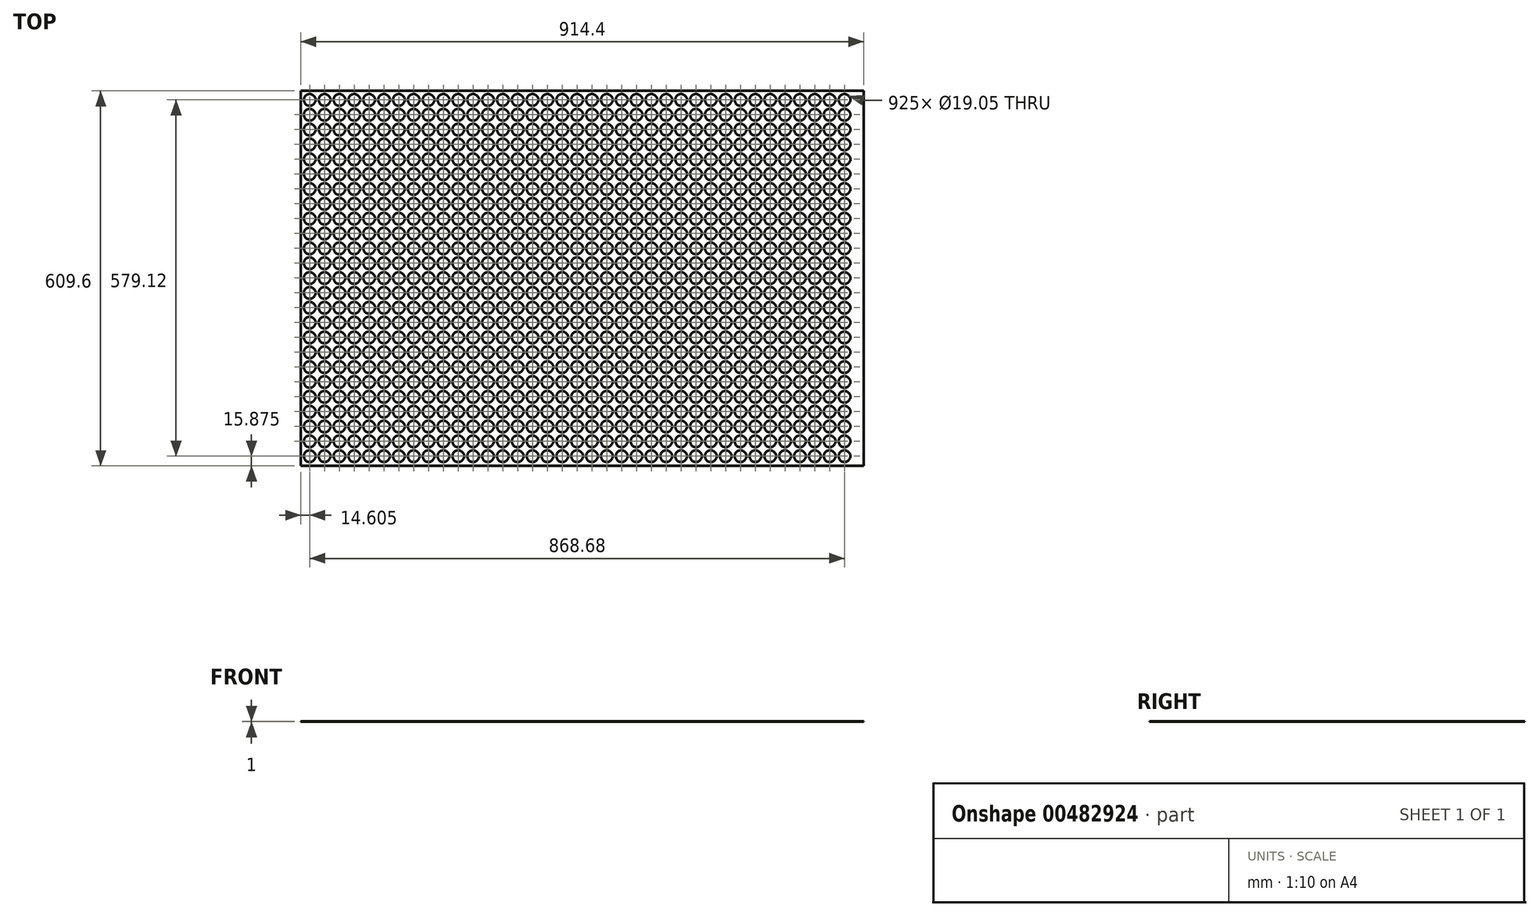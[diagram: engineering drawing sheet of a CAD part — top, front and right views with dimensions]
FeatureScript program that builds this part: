
annotation { "Feature Type Name" : "Feature", "Feature Type Description" : "" }
export const myFeature = defineFeature(function(context is Context, id is Id, definition is map)
    precondition{}
    {
        {
            var Q0;
            Q0=qCreatedBy(makeId("Top.planeOp"),FACE);
            var sketch = newSketch(context, id + "F0", { "sketchPlane" : qUnion([Q0])});
            skLineSegment(sketch, "E0.bottom", {"start": v(-457.2, 304.8) * mm, "end": v(457.2, 304.8) * mm});
            skLineSegment(sketch, "E0.top", {"start": v(-457.2, -304.8) * mm, "end": v(457.2, -304.8) * mm});
            skLineSegment(sketch, "E0.left", {"start": v(-457.2, 304.8) * mm, "end": v(-457.2, -304.8) * mm});
            skLineSegment(sketch, "E0.right", {"start": v(457.2, 304.8) * mm, "end": v(457.2, -304.8) * mm});
            skCircle(sketch, "E1", {"center": v(-442.6, 290.2) * mm, "radius": 9.53 * mm});
            skCircle(sketch, "E2.0.1.0", {"center": v(-442.6, 266.07) * mm, "radius": 9.53 * mm});
            skCircle(sketch, "E2.0.2.0", {"center": v(-442.6, 241.94) * mm, "radius": 9.53 * mm});
            skCircle(sketch, "E2.0.3.0", {"center": v(-442.6, 217.8) * mm, "radius": 9.53 * mm});
            skCircle(sketch, "E2.0.4.0", {"center": v(-442.6, 193.68) * mm, "radius": 9.53 * mm});
            skCircle(sketch, "E2.0.5.0", {"center": v(-442.6, 169.55) * mm, "radius": 9.53 * mm});
            skCircle(sketch, "E2.0.6.0", {"center": v(-442.6, 145.42) * mm, "radius": 9.53 * mm});
            skCircle(sketch, "E2.0.7.0", {"center": v(-442.6, 121.29) * mm, "radius": 9.53 * mm});
            skCircle(sketch, "E2.0.8.0", {"center": v(-442.6, 97.16) * mm, "radius": 9.53 * mm});
            skCircle(sketch, "E2.0.9.0", {"center": v(-442.6, 73.03) * mm, "radius": 9.53 * mm});
            skCircle(sketch, "E2.0.10.0", {"center": v(-442.6, 48.9) * mm, "radius": 9.53 * mm});
            skCircle(sketch, "E2.0.11.0", {"center": v(-442.6, 24.77) * mm, "radius": 9.53 * mm});
            skCircle(sketch, "E2.0.12.0", {"center": v(-442.6, 0.64) * mm, "radius": 9.53 * mm});
            skCircle(sketch, "E2.0.13.0", {"center": v(-442.6, -23.5) * mm, "radius": 9.53 * mm});
            skCircle(sketch, "E2.0.14.0", {"center": v(-442.6, -47.62) * mm, "radius": 9.53 * mm});
            skCircle(sketch, "E2.0.15.0", {"center": v(-442.6, -71.75) * mm, "radius": 9.53 * mm});
            skCircle(sketch, "E2.0.16.0", {"center": v(-442.6, -95.88) * mm, "radius": 9.53 * mm});
            skCircle(sketch, "E2.0.17.0", {"center": v(-442.6, -120.01) * mm, "radius": 9.53 * mm});
            skCircle(sketch, "E2.0.18.0", {"center": v(-442.6, -144.14) * mm, "radius": 9.53 * mm});
            skCircle(sketch, "E2.0.19.0", {"center": v(-442.6, -168.27) * mm, "radius": 9.53 * mm});
            skCircle(sketch, "E2.0.20.0", {"center": v(-442.6, -192.4) * mm, "radius": 9.53 * mm});
            skCircle(sketch, "E2.0.21.0", {"center": v(-442.6, -216.53) * mm, "radius": 9.53 * mm});
            skCircle(sketch, "E2.0.22.0", {"center": v(-442.6, -240.66) * mm, "radius": 9.53 * mm});
            skCircle(sketch, "E2.0.23.0", {"center": v(-442.6, -264.8) * mm, "radius": 9.53 * mm});
            skCircle(sketch, "E2.0.24.0", {"center": v(-442.6, -288.92) * mm, "radius": 9.53 * mm});
            skCircle(sketch, "E2.1.0.0", {"center": v(-418.47, 290.2) * mm, "radius": 9.53 * mm});
            skCircle(sketch, "E2.1.1.0", {"center": v(-418.47, 266.07) * mm, "radius": 9.53 * mm});
            skCircle(sketch, "E2.1.2.0", {"center": v(-418.47, 241.94) * mm, "radius": 9.53 * mm});
            skCircle(sketch, "E2.1.3.0", {"center": v(-418.47, 217.8) * mm, "radius": 9.53 * mm});
            skCircle(sketch, "E2.1.4.0", {"center": v(-418.47, 193.68) * mm, "radius": 9.53 * mm});
            skCircle(sketch, "E2.1.5.0", {"center": v(-418.47, 169.55) * mm, "radius": 9.53 * mm});
            skCircle(sketch, "E2.1.6.0", {"center": v(-418.47, 145.42) * mm, "radius": 9.53 * mm});
            skCircle(sketch, "E2.1.7.0", {"center": v(-418.47, 121.29) * mm, "radius": 9.53 * mm});
            skCircle(sketch, "E2.1.8.0", {"center": v(-418.47, 97.16) * mm, "radius": 9.53 * mm});
            skCircle(sketch, "E2.1.9.0", {"center": v(-418.47, 73.03) * mm, "radius": 9.53 * mm});
            skCircle(sketch, "E2.1.10.0", {"center": v(-418.47, 48.9) * mm, "radius": 9.53 * mm});
            skCircle(sketch, "E2.1.11.0", {"center": v(-418.47, 24.77) * mm, "radius": 9.53 * mm});
            skCircle(sketch, "E2.1.12.0", {"center": v(-418.47, 0.64) * mm, "radius": 9.53 * mm});
            skCircle(sketch, "E2.1.13.0", {"center": v(-418.47, -23.5) * mm, "radius": 9.53 * mm});
            skCircle(sketch, "E2.1.14.0", {"center": v(-418.47, -47.62) * mm, "radius": 9.53 * mm});
            skCircle(sketch, "E2.1.15.0", {"center": v(-418.47, -71.75) * mm, "radius": 9.53 * mm});
            skCircle(sketch, "E2.1.16.0", {"center": v(-418.47, -95.88) * mm, "radius": 9.53 * mm});
            skCircle(sketch, "E2.1.17.0", {"center": v(-418.47, -120.01) * mm, "radius": 9.53 * mm});
            skCircle(sketch, "E2.1.18.0", {"center": v(-418.47, -144.14) * mm, "radius": 9.53 * mm});
            skCircle(sketch, "E2.1.19.0", {"center": v(-418.47, -168.27) * mm, "radius": 9.53 * mm});
            skCircle(sketch, "E2.1.20.0", {"center": v(-418.47, -192.4) * mm, "radius": 9.53 * mm});
            skCircle(sketch, "E2.1.21.0", {"center": v(-418.47, -216.53) * mm, "radius": 9.53 * mm});
            skCircle(sketch, "E2.1.22.0", {"center": v(-418.47, -240.66) * mm, "radius": 9.53 * mm});
            skCircle(sketch, "E2.1.23.0", {"center": v(-418.47, -264.8) * mm, "radius": 9.53 * mm});
            skCircle(sketch, "E2.1.24.0", {"center": v(-418.47, -288.92) * mm, "radius": 9.53 * mm});
            skCircle(sketch, "E2.2.0.0", {"center": v(-394.34, 290.2) * mm, "radius": 9.53 * mm});
            skCircle(sketch, "E2.2.1.0", {"center": v(-394.34, 266.07) * mm, "radius": 9.53 * mm});
            skCircle(sketch, "E2.2.2.0", {"center": v(-394.34, 241.94) * mm, "radius": 9.53 * mm});
            skCircle(sketch, "E2.2.3.0", {"center": v(-394.34, 217.8) * mm, "radius": 9.53 * mm});
            skCircle(sketch, "E2.2.4.0", {"center": v(-394.34, 193.68) * mm, "radius": 9.53 * mm});
            skCircle(sketch, "E2.2.5.0", {"center": v(-394.34, 169.55) * mm, "radius": 9.53 * mm});
            skCircle(sketch, "E2.2.6.0", {"center": v(-394.34, 145.42) * mm, "radius": 9.53 * mm});
            skCircle(sketch, "E2.2.7.0", {"center": v(-394.34, 121.29) * mm, "radius": 9.53 * mm});
            skCircle(sketch, "E2.2.8.0", {"center": v(-394.34, 97.16) * mm, "radius": 9.53 * mm});
            skCircle(sketch, "E2.2.9.0", {"center": v(-394.34, 73.03) * mm, "radius": 9.53 * mm});
            skCircle(sketch, "E2.2.10.0", {"center": v(-394.34, 48.9) * mm, "radius": 9.53 * mm});
            skCircle(sketch, "E2.2.11.0", {"center": v(-394.34, 24.77) * mm, "radius": 9.53 * mm});
            skCircle(sketch, "E2.2.12.0", {"center": v(-394.34, 0.64) * mm, "radius": 9.53 * mm});
            skCircle(sketch, "E2.2.13.0", {"center": v(-394.34, -23.5) * mm, "radius": 9.53 * mm});
            skCircle(sketch, "E2.2.14.0", {"center": v(-394.34, -47.62) * mm, "radius": 9.53 * mm});
            skCircle(sketch, "E2.2.15.0", {"center": v(-394.34, -71.75) * mm, "radius": 9.53 * mm});
            skCircle(sketch, "E2.2.16.0", {"center": v(-394.34, -95.88) * mm, "radius": 9.53 * mm});
            skCircle(sketch, "E2.2.17.0", {"center": v(-394.34, -120.01) * mm, "radius": 9.53 * mm});
            skCircle(sketch, "E2.2.18.0", {"center": v(-394.34, -144.14) * mm, "radius": 9.53 * mm});
            skCircle(sketch, "E2.2.19.0", {"center": v(-394.34, -168.27) * mm, "radius": 9.53 * mm});
            skCircle(sketch, "E2.2.20.0", {"center": v(-394.34, -192.4) * mm, "radius": 9.53 * mm});
            skCircle(sketch, "E2.2.21.0", {"center": v(-394.34, -216.53) * mm, "radius": 9.53 * mm});
            skCircle(sketch, "E2.2.22.0", {"center": v(-394.34, -240.66) * mm, "radius": 9.53 * mm});
            skCircle(sketch, "E2.2.23.0", {"center": v(-394.34, -264.8) * mm, "radius": 9.53 * mm});
            skCircle(sketch, "E2.2.24.0", {"center": v(-394.34, -288.92) * mm, "radius": 9.53 * mm});
            skCircle(sketch, "E2.3.0.0", {"center": v(-370.2, 290.2) * mm, "radius": 9.53 * mm});
            skCircle(sketch, "E2.3.1.0", {"center": v(-370.2, 266.07) * mm, "radius": 9.53 * mm});
            skCircle(sketch, "E2.3.2.0", {"center": v(-370.2, 241.94) * mm, "radius": 9.53 * mm});
            skCircle(sketch, "E2.3.3.0", {"center": v(-370.2, 217.8) * mm, "radius": 9.53 * mm});
            skCircle(sketch, "E2.3.4.0", {"center": v(-370.2, 193.68) * mm, "radius": 9.53 * mm});
            skCircle(sketch, "E2.3.5.0", {"center": v(-370.2, 169.55) * mm, "radius": 9.53 * mm});
            skCircle(sketch, "E2.3.6.0", {"center": v(-370.2, 145.42) * mm, "radius": 9.53 * mm});
            skCircle(sketch, "E2.3.7.0", {"center": v(-370.2, 121.29) * mm, "radius": 9.53 * mm});
            skCircle(sketch, "E2.3.8.0", {"center": v(-370.2, 97.16) * mm, "radius": 9.53 * mm});
            skCircle(sketch, "E2.3.9.0", {"center": v(-370.2, 73.03) * mm, "radius": 9.53 * mm});
            skCircle(sketch, "E2.3.10.0", {"center": v(-370.2, 48.9) * mm, "radius": 9.53 * mm});
            skCircle(sketch, "E2.3.11.0", {"center": v(-370.2, 24.77) * mm, "radius": 9.53 * mm});
            skCircle(sketch, "E2.3.12.0", {"center": v(-370.2, 0.64) * mm, "radius": 9.53 * mm});
            skCircle(sketch, "E2.3.13.0", {"center": v(-370.2, -23.5) * mm, "radius": 9.53 * mm});
            skCircle(sketch, "E2.3.14.0", {"center": v(-370.2, -47.62) * mm, "radius": 9.53 * mm});
            skCircle(sketch, "E2.3.15.0", {"center": v(-370.2, -71.75) * mm, "radius": 9.53 * mm});
            skCircle(sketch, "E2.3.16.0", {"center": v(-370.2, -95.88) * mm, "radius": 9.53 * mm});
            skCircle(sketch, "E2.3.17.0", {"center": v(-370.2, -120.01) * mm, "radius": 9.53 * mm});
            skCircle(sketch, "E2.3.18.0", {"center": v(-370.2, -144.14) * mm, "radius": 9.53 * mm});
            skCircle(sketch, "E2.3.19.0", {"center": v(-370.2, -168.27) * mm, "radius": 9.53 * mm});
            skCircle(sketch, "E2.3.20.0", {"center": v(-370.2, -192.4) * mm, "radius": 9.53 * mm});
            skCircle(sketch, "E2.3.21.0", {"center": v(-370.2, -216.53) * mm, "radius": 9.53 * mm});
            skCircle(sketch, "E2.3.22.0", {"center": v(-370.2, -240.66) * mm, "radius": 9.53 * mm});
            skCircle(sketch, "E2.3.23.0", {"center": v(-370.2, -264.8) * mm, "radius": 9.53 * mm});
            skCircle(sketch, "E2.3.24.0", {"center": v(-370.2, -288.92) * mm, "radius": 9.53 * mm});
            skCircle(sketch, "E2.4.0.0", {"center": v(-346.08, 290.2) * mm, "radius": 9.53 * mm});
            skCircle(sketch, "E2.4.1.0", {"center": v(-346.08, 266.07) * mm, "radius": 9.53 * mm});
            skCircle(sketch, "E2.4.2.0", {"center": v(-346.08, 241.94) * mm, "radius": 9.53 * mm});
            skCircle(sketch, "E2.4.3.0", {"center": v(-346.08, 217.8) * mm, "radius": 9.53 * mm});
            skCircle(sketch, "E2.4.4.0", {"center": v(-346.08, 193.68) * mm, "radius": 9.53 * mm});
            skCircle(sketch, "E2.4.5.0", {"center": v(-346.08, 169.55) * mm, "radius": 9.53 * mm});
            skCircle(sketch, "E2.4.6.0", {"center": v(-346.08, 145.42) * mm, "radius": 9.53 * mm});
            skCircle(sketch, "E2.4.7.0", {"center": v(-346.08, 121.29) * mm, "radius": 9.53 * mm});
            skCircle(sketch, "E2.4.8.0", {"center": v(-346.08, 97.16) * mm, "radius": 9.53 * mm});
            skCircle(sketch, "E2.4.9.0", {"center": v(-346.08, 73.03) * mm, "radius": 9.53 * mm});
            skCircle(sketch, "E2.4.10.0", {"center": v(-346.08, 48.9) * mm, "radius": 9.53 * mm});
            skCircle(sketch, "E2.4.11.0", {"center": v(-346.08, 24.77) * mm, "radius": 9.53 * mm});
            skCircle(sketch, "E2.4.12.0", {"center": v(-346.08, 0.64) * mm, "radius": 9.53 * mm});
            skCircle(sketch, "E2.4.13.0", {"center": v(-346.08, -23.5) * mm, "radius": 9.53 * mm});
            skCircle(sketch, "E2.4.14.0", {"center": v(-346.08, -47.62) * mm, "radius": 9.53 * mm});
            skCircle(sketch, "E2.4.15.0", {"center": v(-346.08, -71.75) * mm, "radius": 9.53 * mm});
            skCircle(sketch, "E2.4.16.0", {"center": v(-346.08, -95.88) * mm, "radius": 9.53 * mm});
            skCircle(sketch, "E2.4.17.0", {"center": v(-346.08, -120.01) * mm, "radius": 9.53 * mm});
            skCircle(sketch, "E2.4.18.0", {"center": v(-346.08, -144.14) * mm, "radius": 9.53 * mm});
            skCircle(sketch, "E2.4.19.0", {"center": v(-346.08, -168.27) * mm, "radius": 9.53 * mm});
            skCircle(sketch, "E2.4.20.0", {"center": v(-346.08, -192.4) * mm, "radius": 9.53 * mm});
            skCircle(sketch, "E2.4.21.0", {"center": v(-346.08, -216.53) * mm, "radius": 9.53 * mm});
            skCircle(sketch, "E2.4.22.0", {"center": v(-346.08, -240.66) * mm, "radius": 9.53 * mm});
            skCircle(sketch, "E2.4.23.0", {"center": v(-346.08, -264.8) * mm, "radius": 9.53 * mm});
            skCircle(sketch, "E2.4.24.0", {"center": v(-346.08, -288.92) * mm, "radius": 9.53 * mm});
            skCircle(sketch, "E2.5.0.0", {"center": v(-321.95, 290.2) * mm, "radius": 9.53 * mm});
            skCircle(sketch, "E2.5.1.0", {"center": v(-321.95, 266.07) * mm, "radius": 9.53 * mm});
            skCircle(sketch, "E2.5.2.0", {"center": v(-321.95, 241.94) * mm, "radius": 9.53 * mm});
            skCircle(sketch, "E2.5.3.0", {"center": v(-321.95, 217.8) * mm, "radius": 9.53 * mm});
            skCircle(sketch, "E2.5.4.0", {"center": v(-321.95, 193.68) * mm, "radius": 9.53 * mm});
            skCircle(sketch, "E2.5.5.0", {"center": v(-321.95, 169.55) * mm, "radius": 9.53 * mm});
            skCircle(sketch, "E2.5.6.0", {"center": v(-321.95, 145.42) * mm, "radius": 9.53 * mm});
            skCircle(sketch, "E2.5.7.0", {"center": v(-321.95, 121.29) * mm, "radius": 9.53 * mm});
            skCircle(sketch, "E2.5.8.0", {"center": v(-321.95, 97.16) * mm, "radius": 9.53 * mm});
            skCircle(sketch, "E2.5.9.0", {"center": v(-321.95, 73.03) * mm, "radius": 9.53 * mm});
            skCircle(sketch, "E2.5.10.0", {"center": v(-321.95, 48.9) * mm, "radius": 9.53 * mm});
            skCircle(sketch, "E2.5.11.0", {"center": v(-321.95, 24.77) * mm, "radius": 9.53 * mm});
            skCircle(sketch, "E2.5.12.0", {"center": v(-321.95, 0.64) * mm, "radius": 9.53 * mm});
            skCircle(sketch, "E2.5.13.0", {"center": v(-321.95, -23.5) * mm, "radius": 9.53 * mm});
            skCircle(sketch, "E2.5.14.0", {"center": v(-321.95, -47.62) * mm, "radius": 9.53 * mm});
            skCircle(sketch, "E2.5.15.0", {"center": v(-321.95, -71.75) * mm, "radius": 9.53 * mm});
            skCircle(sketch, "E2.5.16.0", {"center": v(-321.95, -95.88) * mm, "radius": 9.53 * mm});
            skCircle(sketch, "E2.5.17.0", {"center": v(-321.95, -120.01) * mm, "radius": 9.53 * mm});
            skCircle(sketch, "E2.5.18.0", {"center": v(-321.95, -144.14) * mm, "radius": 9.53 * mm});
            skCircle(sketch, "E2.5.19.0", {"center": v(-321.95, -168.27) * mm, "radius": 9.53 * mm});
            skCircle(sketch, "E2.5.20.0", {"center": v(-321.95, -192.4) * mm, "radius": 9.53 * mm});
            skCircle(sketch, "E2.5.21.0", {"center": v(-321.95, -216.53) * mm, "radius": 9.53 * mm});
            skCircle(sketch, "E2.5.22.0", {"center": v(-321.95, -240.66) * mm, "radius": 9.53 * mm});
            skCircle(sketch, "E2.5.23.0", {"center": v(-321.95, -264.8) * mm, "radius": 9.53 * mm});
            skCircle(sketch, "E2.5.24.0", {"center": v(-321.95, -288.92) * mm, "radius": 9.53 * mm});
            skCircle(sketch, "E2.6.0.0", {"center": v(-297.82, 290.2) * mm, "radius": 9.53 * mm});
            skCircle(sketch, "E2.6.1.0", {"center": v(-297.82, 266.07) * mm, "radius": 9.53 * mm});
            skCircle(sketch, "E2.6.2.0", {"center": v(-297.82, 241.94) * mm, "radius": 9.53 * mm});
            skCircle(sketch, "E2.6.3.0", {"center": v(-297.82, 217.8) * mm, "radius": 9.53 * mm});
            skCircle(sketch, "E2.6.4.0", {"center": v(-297.82, 193.68) * mm, "radius": 9.53 * mm});
            skCircle(sketch, "E2.6.5.0", {"center": v(-297.82, 169.55) * mm, "radius": 9.53 * mm});
            skCircle(sketch, "E2.6.6.0", {"center": v(-297.82, 145.42) * mm, "radius": 9.53 * mm});
            skCircle(sketch, "E2.6.7.0", {"center": v(-297.82, 121.29) * mm, "radius": 9.53 * mm});
            skCircle(sketch, "E2.6.8.0", {"center": v(-297.82, 97.16) * mm, "radius": 9.53 * mm});
            skCircle(sketch, "E2.6.9.0", {"center": v(-297.82, 73.03) * mm, "radius": 9.53 * mm});
            skCircle(sketch, "E2.6.10.0", {"center": v(-297.82, 48.9) * mm, "radius": 9.53 * mm});
            skCircle(sketch, "E2.6.11.0", {"center": v(-297.82, 24.77) * mm, "radius": 9.53 * mm});
            skCircle(sketch, "E2.6.12.0", {"center": v(-297.82, 0.64) * mm, "radius": 9.53 * mm});
            skCircle(sketch, "E2.6.13.0", {"center": v(-297.82, -23.5) * mm, "radius": 9.53 * mm});
            skCircle(sketch, "E2.6.14.0", {"center": v(-297.82, -47.62) * mm, "radius": 9.53 * mm});
            skCircle(sketch, "E2.6.15.0", {"center": v(-297.82, -71.75) * mm, "radius": 9.53 * mm});
            skCircle(sketch, "E2.6.16.0", {"center": v(-297.82, -95.88) * mm, "radius": 9.53 * mm});
            skCircle(sketch, "E2.6.17.0", {"center": v(-297.82, -120.01) * mm, "radius": 9.53 * mm});
            skCircle(sketch, "E2.6.18.0", {"center": v(-297.82, -144.14) * mm, "radius": 9.53 * mm});
            skCircle(sketch, "E2.6.19.0", {"center": v(-297.82, -168.27) * mm, "radius": 9.53 * mm});
            skCircle(sketch, "E2.6.20.0", {"center": v(-297.82, -192.4) * mm, "radius": 9.53 * mm});
            skCircle(sketch, "E2.6.21.0", {"center": v(-297.82, -216.53) * mm, "radius": 9.53 * mm});
            skCircle(sketch, "E2.6.22.0", {"center": v(-297.82, -240.66) * mm, "radius": 9.53 * mm});
            skCircle(sketch, "E2.6.23.0", {"center": v(-297.82, -264.8) * mm, "radius": 9.53 * mm});
            skCircle(sketch, "E2.6.24.0", {"center": v(-297.82, -288.92) * mm, "radius": 9.53 * mm});
            skCircle(sketch, "E2.7.0.0", {"center": v(-273.69, 290.2) * mm, "radius": 9.53 * mm});
            skCircle(sketch, "E2.7.1.0", {"center": v(-273.69, 266.07) * mm, "radius": 9.53 * mm});
            skCircle(sketch, "E2.7.2.0", {"center": v(-273.69, 241.94) * mm, "radius": 9.53 * mm});
            skCircle(sketch, "E2.7.3.0", {"center": v(-273.69, 217.8) * mm, "radius": 9.53 * mm});
            skCircle(sketch, "E2.7.4.0", {"center": v(-273.69, 193.68) * mm, "radius": 9.53 * mm});
            skCircle(sketch, "E2.7.5.0", {"center": v(-273.69, 169.55) * mm, "radius": 9.53 * mm});
            skCircle(sketch, "E2.7.6.0", {"center": v(-273.69, 145.42) * mm, "radius": 9.53 * mm});
            skCircle(sketch, "E2.7.7.0", {"center": v(-273.69, 121.29) * mm, "radius": 9.53 * mm});
            skCircle(sketch, "E2.7.8.0", {"center": v(-273.69, 97.16) * mm, "radius": 9.53 * mm});
            skCircle(sketch, "E2.7.9.0", {"center": v(-273.69, 73.03) * mm, "radius": 9.53 * mm});
            skCircle(sketch, "E2.7.10.0", {"center": v(-273.69, 48.9) * mm, "radius": 9.53 * mm});
            skCircle(sketch, "E2.7.11.0", {"center": v(-273.69, 24.77) * mm, "radius": 9.53 * mm});
            skCircle(sketch, "E2.7.12.0", {"center": v(-273.69, 0.64) * mm, "radius": 9.53 * mm});
            skCircle(sketch, "E2.7.13.0", {"center": v(-273.69, -23.5) * mm, "radius": 9.53 * mm});
            skCircle(sketch, "E2.7.14.0", {"center": v(-273.69, -47.62) * mm, "radius": 9.53 * mm});
            skCircle(sketch, "E2.7.15.0", {"center": v(-273.69, -71.75) * mm, "radius": 9.53 * mm});
            skCircle(sketch, "E2.7.16.0", {"center": v(-273.69, -95.88) * mm, "radius": 9.53 * mm});
            skCircle(sketch, "E2.7.17.0", {"center": v(-273.69, -120.01) * mm, "radius": 9.53 * mm});
            skCircle(sketch, "E2.7.18.0", {"center": v(-273.69, -144.14) * mm, "radius": 9.53 * mm});
            skCircle(sketch, "E2.7.19.0", {"center": v(-273.69, -168.27) * mm, "radius": 9.53 * mm});
            skCircle(sketch, "E2.7.20.0", {"center": v(-273.69, -192.4) * mm, "radius": 9.53 * mm});
            skCircle(sketch, "E2.7.21.0", {"center": v(-273.69, -216.53) * mm, "radius": 9.53 * mm});
            skCircle(sketch, "E2.7.22.0", {"center": v(-273.69, -240.66) * mm, "radius": 9.53 * mm});
            skCircle(sketch, "E2.7.23.0", {"center": v(-273.69, -264.8) * mm, "radius": 9.53 * mm});
            skCircle(sketch, "E2.7.24.0", {"center": v(-273.69, -288.92) * mm, "radius": 9.53 * mm});
            skCircle(sketch, "E2.8.0.0", {"center": v(-249.56, 290.2) * mm, "radius": 9.53 * mm});
            skCircle(sketch, "E2.8.1.0", {"center": v(-249.56, 266.07) * mm, "radius": 9.53 * mm});
            skCircle(sketch, "E2.8.2.0", {"center": v(-249.56, 241.94) * mm, "radius": 9.53 * mm});
            skCircle(sketch, "E2.8.3.0", {"center": v(-249.56, 217.8) * mm, "radius": 9.53 * mm});
            skCircle(sketch, "E2.8.4.0", {"center": v(-249.56, 193.68) * mm, "radius": 9.53 * mm});
            skCircle(sketch, "E2.8.5.0", {"center": v(-249.56, 169.55) * mm, "radius": 9.53 * mm});
            skCircle(sketch, "E2.8.6.0", {"center": v(-249.56, 145.42) * mm, "radius": 9.53 * mm});
            skCircle(sketch, "E2.8.7.0", {"center": v(-249.56, 121.29) * mm, "radius": 9.53 * mm});
            skCircle(sketch, "E2.8.8.0", {"center": v(-249.56, 97.16) * mm, "radius": 9.53 * mm});
            skCircle(sketch, "E2.8.9.0", {"center": v(-249.56, 73.03) * mm, "radius": 9.53 * mm});
            skCircle(sketch, "E2.8.10.0", {"center": v(-249.56, 48.9) * mm, "radius": 9.53 * mm});
            skCircle(sketch, "E2.8.11.0", {"center": v(-249.56, 24.77) * mm, "radius": 9.53 * mm});
            skCircle(sketch, "E2.8.12.0", {"center": v(-249.56, 0.64) * mm, "radius": 9.53 * mm});
            skCircle(sketch, "E2.8.13.0", {"center": v(-249.56, -23.5) * mm, "radius": 9.53 * mm});
            skCircle(sketch, "E2.8.14.0", {"center": v(-249.56, -47.62) * mm, "radius": 9.53 * mm});
            skCircle(sketch, "E2.8.15.0", {"center": v(-249.56, -71.75) * mm, "radius": 9.53 * mm});
            skCircle(sketch, "E2.8.16.0", {"center": v(-249.56, -95.88) * mm, "radius": 9.53 * mm});
            skCircle(sketch, "E2.8.17.0", {"center": v(-249.56, -120.01) * mm, "radius": 9.53 * mm});
            skCircle(sketch, "E2.8.18.0", {"center": v(-249.56, -144.14) * mm, "radius": 9.53 * mm});
            skCircle(sketch, "E2.8.19.0", {"center": v(-249.56, -168.27) * mm, "radius": 9.53 * mm});
            skCircle(sketch, "E2.8.20.0", {"center": v(-249.56, -192.4) * mm, "radius": 9.53 * mm});
            skCircle(sketch, "E2.8.21.0", {"center": v(-249.56, -216.53) * mm, "radius": 9.53 * mm});
            skCircle(sketch, "E2.8.22.0", {"center": v(-249.56, -240.66) * mm, "radius": 9.53 * mm});
            skCircle(sketch, "E2.8.23.0", {"center": v(-249.56, -264.8) * mm, "radius": 9.53 * mm});
            skCircle(sketch, "E2.8.24.0", {"center": v(-249.56, -288.92) * mm, "radius": 9.53 * mm});
            skCircle(sketch, "E2.9.0.0", {"center": v(-225.43, 290.2) * mm, "radius": 9.53 * mm});
            skCircle(sketch, "E2.9.1.0", {"center": v(-225.43, 266.07) * mm, "radius": 9.53 * mm});
            skCircle(sketch, "E2.9.2.0", {"center": v(-225.43, 241.94) * mm, "radius": 9.53 * mm});
            skCircle(sketch, "E2.9.3.0", {"center": v(-225.43, 217.8) * mm, "radius": 9.53 * mm});
            skCircle(sketch, "E2.9.4.0", {"center": v(-225.43, 193.68) * mm, "radius": 9.53 * mm});
            skCircle(sketch, "E2.9.5.0", {"center": v(-225.43, 169.55) * mm, "radius": 9.53 * mm});
            skCircle(sketch, "E2.9.6.0", {"center": v(-225.43, 145.42) * mm, "radius": 9.53 * mm});
            skCircle(sketch, "E2.9.7.0", {"center": v(-225.43, 121.29) * mm, "radius": 9.53 * mm});
            skCircle(sketch, "E2.9.8.0", {"center": v(-225.43, 97.16) * mm, "radius": 9.53 * mm});
            skCircle(sketch, "E2.9.9.0", {"center": v(-225.43, 73.03) * mm, "radius": 9.53 * mm});
            skCircle(sketch, "E2.9.10.0", {"center": v(-225.43, 48.9) * mm, "radius": 9.53 * mm});
            skCircle(sketch, "E2.9.11.0", {"center": v(-225.43, 24.77) * mm, "radius": 9.53 * mm});
            skCircle(sketch, "E2.9.12.0", {"center": v(-225.43, 0.64) * mm, "radius": 9.53 * mm});
            skCircle(sketch, "E2.9.13.0", {"center": v(-225.43, -23.5) * mm, "radius": 9.53 * mm});
            skCircle(sketch, "E2.9.14.0", {"center": v(-225.43, -47.62) * mm, "radius": 9.53 * mm});
            skCircle(sketch, "E2.9.15.0", {"center": v(-225.43, -71.75) * mm, "radius": 9.53 * mm});
            skCircle(sketch, "E2.9.16.0", {"center": v(-225.43, -95.88) * mm, "radius": 9.53 * mm});
            skCircle(sketch, "E2.9.17.0", {"center": v(-225.43, -120.01) * mm, "radius": 9.53 * mm});
            skCircle(sketch, "E2.9.18.0", {"center": v(-225.43, -144.14) * mm, "radius": 9.53 * mm});
            skCircle(sketch, "E2.9.19.0", {"center": v(-225.43, -168.27) * mm, "radius": 9.53 * mm});
            skCircle(sketch, "E2.9.20.0", {"center": v(-225.43, -192.4) * mm, "radius": 9.53 * mm});
            skCircle(sketch, "E2.9.21.0", {"center": v(-225.43, -216.53) * mm, "radius": 9.53 * mm});
            skCircle(sketch, "E2.9.22.0", {"center": v(-225.43, -240.66) * mm, "radius": 9.53 * mm});
            skCircle(sketch, "E2.9.23.0", {"center": v(-225.43, -264.8) * mm, "radius": 9.53 * mm});
            skCircle(sketch, "E2.9.24.0", {"center": v(-225.43, -288.92) * mm, "radius": 9.53 * mm});
            skCircle(sketch, "E2.10.0.0", {"center": v(-201.3, 290.2) * mm, "radius": 9.53 * mm});
            skCircle(sketch, "E2.10.1.0", {"center": v(-201.3, 266.07) * mm, "radius": 9.53 * mm});
            skCircle(sketch, "E2.10.2.0", {"center": v(-201.3, 241.94) * mm, "radius": 9.53 * mm});
            skCircle(sketch, "E2.10.3.0", {"center": v(-201.3, 217.8) * mm, "radius": 9.53 * mm});
            skCircle(sketch, "E2.10.4.0", {"center": v(-201.3, 193.68) * mm, "radius": 9.53 * mm});
            skCircle(sketch, "E2.10.5.0", {"center": v(-201.3, 169.55) * mm, "radius": 9.53 * mm});
            skCircle(sketch, "E2.10.6.0", {"center": v(-201.3, 145.42) * mm, "radius": 9.53 * mm});
            skCircle(sketch, "E2.10.7.0", {"center": v(-201.3, 121.29) * mm, "radius": 9.53 * mm});
            skCircle(sketch, "E2.10.8.0", {"center": v(-201.3, 97.16) * mm, "radius": 9.53 * mm});
            skCircle(sketch, "E2.10.9.0", {"center": v(-201.3, 73.03) * mm, "radius": 9.53 * mm});
            skCircle(sketch, "E2.10.10.0", {"center": v(-201.3, 48.9) * mm, "radius": 9.53 * mm});
            skCircle(sketch, "E2.10.11.0", {"center": v(-201.3, 24.77) * mm, "radius": 9.53 * mm});
            skCircle(sketch, "E2.10.12.0", {"center": v(-201.3, 0.64) * mm, "radius": 9.53 * mm});
            skCircle(sketch, "E2.10.13.0", {"center": v(-201.3, -23.5) * mm, "radius": 9.53 * mm});
            skCircle(sketch, "E2.10.14.0", {"center": v(-201.3, -47.62) * mm, "radius": 9.53 * mm});
            skCircle(sketch, "E2.10.15.0", {"center": v(-201.3, -71.75) * mm, "radius": 9.53 * mm});
            skCircle(sketch, "E2.10.16.0", {"center": v(-201.3, -95.88) * mm, "radius": 9.53 * mm});
            skCircle(sketch, "E2.10.17.0", {"center": v(-201.3, -120.01) * mm, "radius": 9.53 * mm});
            skCircle(sketch, "E2.10.18.0", {"center": v(-201.3, -144.14) * mm, "radius": 9.53 * mm});
            skCircle(sketch, "E2.10.19.0", {"center": v(-201.3, -168.27) * mm, "radius": 9.53 * mm});
            skCircle(sketch, "E2.10.20.0", {"center": v(-201.3, -192.4) * mm, "radius": 9.53 * mm});
            skCircle(sketch, "E2.10.21.0", {"center": v(-201.3, -216.53) * mm, "radius": 9.53 * mm});
            skCircle(sketch, "E2.10.22.0", {"center": v(-201.3, -240.66) * mm, "radius": 9.53 * mm});
            skCircle(sketch, "E2.10.23.0", {"center": v(-201.3, -264.8) * mm, "radius": 9.53 * mm});
            skCircle(sketch, "E2.10.24.0", {"center": v(-201.3, -288.92) * mm, "radius": 9.53 * mm});
            skCircle(sketch, "E2.11.0.0", {"center": v(-177.17, 290.2) * mm, "radius": 9.53 * mm});
            skCircle(sketch, "E2.11.1.0", {"center": v(-177.17, 266.07) * mm, "radius": 9.53 * mm});
            skCircle(sketch, "E2.11.2.0", {"center": v(-177.17, 241.94) * mm, "radius": 9.53 * mm});
            skCircle(sketch, "E2.11.3.0", {"center": v(-177.17, 217.8) * mm, "radius": 9.53 * mm});
            skCircle(sketch, "E2.11.4.0", {"center": v(-177.17, 193.68) * mm, "radius": 9.53 * mm});
            skCircle(sketch, "E2.11.5.0", {"center": v(-177.17, 169.55) * mm, "radius": 9.53 * mm});
            skCircle(sketch, "E2.11.6.0", {"center": v(-177.17, 145.42) * mm, "radius": 9.53 * mm});
            skCircle(sketch, "E2.11.7.0", {"center": v(-177.17, 121.29) * mm, "radius": 9.53 * mm});
            skCircle(sketch, "E2.11.8.0", {"center": v(-177.17, 97.16) * mm, "radius": 9.53 * mm});
            skCircle(sketch, "E2.11.9.0", {"center": v(-177.17, 73.03) * mm, "radius": 9.53 * mm});
            skCircle(sketch, "E2.11.10.0", {"center": v(-177.17, 48.9) * mm, "radius": 9.53 * mm});
            skCircle(sketch, "E2.11.11.0", {"center": v(-177.17, 24.77) * mm, "radius": 9.53 * mm});
            skCircle(sketch, "E2.11.12.0", {"center": v(-177.17, 0.64) * mm, "radius": 9.53 * mm});
            skCircle(sketch, "E2.11.13.0", {"center": v(-177.17, -23.5) * mm, "radius": 9.53 * mm});
            skCircle(sketch, "E2.11.14.0", {"center": v(-177.17, -47.62) * mm, "radius": 9.53 * mm});
            skCircle(sketch, "E2.11.15.0", {"center": v(-177.17, -71.75) * mm, "radius": 9.53 * mm});
            skCircle(sketch, "E2.11.16.0", {"center": v(-177.17, -95.88) * mm, "radius": 9.53 * mm});
            skCircle(sketch, "E2.11.17.0", {"center": v(-177.17, -120.01) * mm, "radius": 9.53 * mm});
            skCircle(sketch, "E2.11.18.0", {"center": v(-177.17, -144.14) * mm, "radius": 9.53 * mm});
            skCircle(sketch, "E2.11.19.0", {"center": v(-177.17, -168.27) * mm, "radius": 9.53 * mm});
            skCircle(sketch, "E2.11.20.0", {"center": v(-177.17, -192.4) * mm, "radius": 9.53 * mm});
            skCircle(sketch, "E2.11.21.0", {"center": v(-177.17, -216.53) * mm, "radius": 9.53 * mm});
            skCircle(sketch, "E2.11.22.0", {"center": v(-177.17, -240.66) * mm, "radius": 9.53 * mm});
            skCircle(sketch, "E2.11.23.0", {"center": v(-177.17, -264.8) * mm, "radius": 9.53 * mm});
            skCircle(sketch, "E2.11.24.0", {"center": v(-177.17, -288.92) * mm, "radius": 9.53 * mm});
            skCircle(sketch, "E2.12.0.0", {"center": v(-153.04, 290.2) * mm, "radius": 9.53 * mm});
            skCircle(sketch, "E2.12.1.0", {"center": v(-153.04, 266.07) * mm, "radius": 9.53 * mm});
            skCircle(sketch, "E2.12.2.0", {"center": v(-153.04, 241.94) * mm, "radius": 9.53 * mm});
            skCircle(sketch, "E2.12.3.0", {"center": v(-153.04, 217.8) * mm, "radius": 9.53 * mm});
            skCircle(sketch, "E2.12.4.0", {"center": v(-153.04, 193.68) * mm, "radius": 9.53 * mm});
            skCircle(sketch, "E2.12.5.0", {"center": v(-153.04, 169.55) * mm, "radius": 9.53 * mm});
            skCircle(sketch, "E2.12.6.0", {"center": v(-153.04, 145.42) * mm, "radius": 9.53 * mm});
            skCircle(sketch, "E2.12.7.0", {"center": v(-153.04, 121.29) * mm, "radius": 9.53 * mm});
            skCircle(sketch, "E2.12.8.0", {"center": v(-153.04, 97.16) * mm, "radius": 9.53 * mm});
            skCircle(sketch, "E2.12.9.0", {"center": v(-153.04, 73.03) * mm, "radius": 9.53 * mm});
            skCircle(sketch, "E2.12.10.0", {"center": v(-153.04, 48.9) * mm, "radius": 9.53 * mm});
            skCircle(sketch, "E2.12.11.0", {"center": v(-153.04, 24.77) * mm, "radius": 9.53 * mm});
            skCircle(sketch, "E2.12.12.0", {"center": v(-153.04, 0.64) * mm, "radius": 9.53 * mm});
            skCircle(sketch, "E2.12.13.0", {"center": v(-153.04, -23.5) * mm, "radius": 9.53 * mm});
            skCircle(sketch, "E2.12.14.0", {"center": v(-153.04, -47.62) * mm, "radius": 9.53 * mm});
            skCircle(sketch, "E2.12.15.0", {"center": v(-153.04, -71.75) * mm, "radius": 9.53 * mm});
            skCircle(sketch, "E2.12.16.0", {"center": v(-153.04, -95.88) * mm, "radius": 9.53 * mm});
            skCircle(sketch, "E2.12.17.0", {"center": v(-153.04, -120.01) * mm, "radius": 9.53 * mm});
            skCircle(sketch, "E2.12.18.0", {"center": v(-153.04, -144.14) * mm, "radius": 9.53 * mm});
            skCircle(sketch, "E2.12.19.0", {"center": v(-153.04, -168.27) * mm, "radius": 9.53 * mm});
            skCircle(sketch, "E2.12.20.0", {"center": v(-153.04, -192.4) * mm, "radius": 9.53 * mm});
            skCircle(sketch, "E2.12.21.0", {"center": v(-153.04, -216.53) * mm, "radius": 9.53 * mm});
            skCircle(sketch, "E2.12.22.0", {"center": v(-153.04, -240.66) * mm, "radius": 9.53 * mm});
            skCircle(sketch, "E2.12.23.0", {"center": v(-153.04, -264.8) * mm, "radius": 9.53 * mm});
            skCircle(sketch, "E2.12.24.0", {"center": v(-153.04, -288.92) * mm, "radius": 9.53 * mm});
            skCircle(sketch, "E2.13.0.0", {"center": v(-128.9, 290.2) * mm, "radius": 9.53 * mm});
            skCircle(sketch, "E2.13.1.0", {"center": v(-128.9, 266.07) * mm, "radius": 9.53 * mm});
            skCircle(sketch, "E2.13.2.0", {"center": v(-128.9, 241.94) * mm, "radius": 9.53 * mm});
            skCircle(sketch, "E2.13.3.0", {"center": v(-128.9, 217.8) * mm, "radius": 9.53 * mm});
            skCircle(sketch, "E2.13.4.0", {"center": v(-128.9, 193.68) * mm, "radius": 9.53 * mm});
            skCircle(sketch, "E2.13.5.0", {"center": v(-128.9, 169.55) * mm, "radius": 9.53 * mm});
            skCircle(sketch, "E2.13.6.0", {"center": v(-128.9, 145.42) * mm, "radius": 9.53 * mm});
            skCircle(sketch, "E2.13.7.0", {"center": v(-128.9, 121.29) * mm, "radius": 9.53 * mm});
            skCircle(sketch, "E2.13.8.0", {"center": v(-128.9, 97.16) * mm, "radius": 9.53 * mm});
            skCircle(sketch, "E2.13.9.0", {"center": v(-128.9, 73.03) * mm, "radius": 9.53 * mm});
            skCircle(sketch, "E2.13.10.0", {"center": v(-128.9, 48.9) * mm, "radius": 9.53 * mm});
            skCircle(sketch, "E2.13.11.0", {"center": v(-128.9, 24.77) * mm, "radius": 9.53 * mm});
            skCircle(sketch, "E2.13.12.0", {"center": v(-128.9, 0.64) * mm, "radius": 9.53 * mm});
            skCircle(sketch, "E2.13.13.0", {"center": v(-128.9, -23.5) * mm, "radius": 9.53 * mm});
            skCircle(sketch, "E2.13.14.0", {"center": v(-128.9, -47.62) * mm, "radius": 9.53 * mm});
            skCircle(sketch, "E2.13.15.0", {"center": v(-128.9, -71.75) * mm, "radius": 9.53 * mm});
            skCircle(sketch, "E2.13.16.0", {"center": v(-128.9, -95.88) * mm, "radius": 9.53 * mm});
            skCircle(sketch, "E2.13.17.0", {"center": v(-128.9, -120.01) * mm, "radius": 9.53 * mm});
            skCircle(sketch, "E2.13.18.0", {"center": v(-128.9, -144.14) * mm, "radius": 9.53 * mm});
            skCircle(sketch, "E2.13.19.0", {"center": v(-128.9, -168.27) * mm, "radius": 9.53 * mm});
            skCircle(sketch, "E2.13.20.0", {"center": v(-128.9, -192.4) * mm, "radius": 9.53 * mm});
            skCircle(sketch, "E2.13.21.0", {"center": v(-128.9, -216.53) * mm, "radius": 9.53 * mm});
            skCircle(sketch, "E2.13.22.0", {"center": v(-128.9, -240.66) * mm, "radius": 9.53 * mm});
            skCircle(sketch, "E2.13.23.0", {"center": v(-128.9, -264.8) * mm, "radius": 9.53 * mm});
            skCircle(sketch, "E2.13.24.0", {"center": v(-128.9, -288.92) * mm, "radius": 9.53 * mm});
            skCircle(sketch, "E2.14.0.0", {"center": v(-104.78, 290.2) * mm, "radius": 9.53 * mm});
            skCircle(sketch, "E2.14.1.0", {"center": v(-104.78, 266.07) * mm, "radius": 9.53 * mm});
            skCircle(sketch, "E2.14.2.0", {"center": v(-104.78, 241.94) * mm, "radius": 9.53 * mm});
            skCircle(sketch, "E2.14.3.0", {"center": v(-104.78, 217.8) * mm, "radius": 9.53 * mm});
            skCircle(sketch, "E2.14.4.0", {"center": v(-104.78, 193.68) * mm, "radius": 9.53 * mm});
            skCircle(sketch, "E2.14.5.0", {"center": v(-104.78, 169.55) * mm, "radius": 9.53 * mm});
            skCircle(sketch, "E2.14.6.0", {"center": v(-104.78, 145.42) * mm, "radius": 9.53 * mm});
            skCircle(sketch, "E2.14.7.0", {"center": v(-104.78, 121.29) * mm, "radius": 9.53 * mm});
            skCircle(sketch, "E2.14.8.0", {"center": v(-104.78, 97.16) * mm, "radius": 9.53 * mm});
            skCircle(sketch, "E2.14.9.0", {"center": v(-104.78, 73.03) * mm, "radius": 9.53 * mm});
            skCircle(sketch, "E2.14.10.0", {"center": v(-104.78, 48.9) * mm, "radius": 9.53 * mm});
            skCircle(sketch, "E2.14.11.0", {"center": v(-104.78, 24.77) * mm, "radius": 9.53 * mm});
            skCircle(sketch, "E2.14.12.0", {"center": v(-104.78, 0.64) * mm, "radius": 9.53 * mm});
            skCircle(sketch, "E2.14.13.0", {"center": v(-104.78, -23.5) * mm, "radius": 9.53 * mm});
            skCircle(sketch, "E2.14.14.0", {"center": v(-104.78, -47.62) * mm, "radius": 9.53 * mm});
            skCircle(sketch, "E2.14.15.0", {"center": v(-104.78, -71.75) * mm, "radius": 9.53 * mm});
            skCircle(sketch, "E2.14.16.0", {"center": v(-104.78, -95.88) * mm, "radius": 9.53 * mm});
            skCircle(sketch, "E2.14.17.0", {"center": v(-104.78, -120.01) * mm, "radius": 9.53 * mm});
            skCircle(sketch, "E2.14.18.0", {"center": v(-104.78, -144.14) * mm, "radius": 9.53 * mm});
            skCircle(sketch, "E2.14.19.0", {"center": v(-104.78, -168.27) * mm, "radius": 9.53 * mm});
            skCircle(sketch, "E2.14.20.0", {"center": v(-104.78, -192.4) * mm, "radius": 9.53 * mm});
            skCircle(sketch, "E2.14.21.0", {"center": v(-104.78, -216.53) * mm, "radius": 9.53 * mm});
            skCircle(sketch, "E2.14.22.0", {"center": v(-104.78, -240.66) * mm, "radius": 9.53 * mm});
            skCircle(sketch, "E2.14.23.0", {"center": v(-104.78, -264.8) * mm, "radius": 9.53 * mm});
            skCircle(sketch, "E2.14.24.0", {"center": v(-104.78, -288.92) * mm, "radius": 9.53 * mm});
            skCircle(sketch, "E2.15.0.0", {"center": v(-80.65, 290.2) * mm, "radius": 9.53 * mm});
            skCircle(sketch, "E2.15.1.0", {"center": v(-80.65, 266.07) * mm, "radius": 9.53 * mm});
            skCircle(sketch, "E2.15.2.0", {"center": v(-80.65, 241.94) * mm, "radius": 9.53 * mm});
            skCircle(sketch, "E2.15.3.0", {"center": v(-80.65, 217.8) * mm, "radius": 9.53 * mm});
            skCircle(sketch, "E2.15.4.0", {"center": v(-80.65, 193.68) * mm, "radius": 9.53 * mm});
            skCircle(sketch, "E2.15.5.0", {"center": v(-80.65, 169.55) * mm, "radius": 9.53 * mm});
            skCircle(sketch, "E2.15.6.0", {"center": v(-80.65, 145.42) * mm, "radius": 9.53 * mm});
            skCircle(sketch, "E2.15.7.0", {"center": v(-80.65, 121.29) * mm, "radius": 9.53 * mm});
            skCircle(sketch, "E2.15.8.0", {"center": v(-80.65, 97.16) * mm, "radius": 9.53 * mm});
            skCircle(sketch, "E2.15.9.0", {"center": v(-80.65, 73.03) * mm, "radius": 9.53 * mm});
            skCircle(sketch, "E2.15.10.0", {"center": v(-80.65, 48.9) * mm, "radius": 9.53 * mm});
            skCircle(sketch, "E2.15.11.0", {"center": v(-80.65, 24.77) * mm, "radius": 9.53 * mm});
            skCircle(sketch, "E2.15.12.0", {"center": v(-80.65, 0.64) * mm, "radius": 9.53 * mm});
            skCircle(sketch, "E2.15.13.0", {"center": v(-80.65, -23.5) * mm, "radius": 9.53 * mm});
            skCircle(sketch, "E2.15.14.0", {"center": v(-80.65, -47.62) * mm, "radius": 9.53 * mm});
            skCircle(sketch, "E2.15.15.0", {"center": v(-80.65, -71.75) * mm, "radius": 9.53 * mm});
            skCircle(sketch, "E2.15.16.0", {"center": v(-80.65, -95.88) * mm, "radius": 9.53 * mm});
            skCircle(sketch, "E2.15.17.0", {"center": v(-80.65, -120.01) * mm, "radius": 9.53 * mm});
            skCircle(sketch, "E2.15.18.0", {"center": v(-80.65, -144.14) * mm, "radius": 9.53 * mm});
            skCircle(sketch, "E2.15.19.0", {"center": v(-80.65, -168.27) * mm, "radius": 9.53 * mm});
            skCircle(sketch, "E2.15.20.0", {"center": v(-80.65, -192.4) * mm, "radius": 9.53 * mm});
            skCircle(sketch, "E2.15.21.0", {"center": v(-80.65, -216.53) * mm, "radius": 9.53 * mm});
            skCircle(sketch, "E2.15.22.0", {"center": v(-80.65, -240.66) * mm, "radius": 9.53 * mm});
            skCircle(sketch, "E2.15.23.0", {"center": v(-80.65, -264.8) * mm, "radius": 9.53 * mm});
            skCircle(sketch, "E2.15.24.0", {"center": v(-80.65, -288.92) * mm, "radius": 9.53 * mm});
            skCircle(sketch, "E2.16.0.0", {"center": v(-56.52, 290.2) * mm, "radius": 9.53 * mm});
            skCircle(sketch, "E2.16.1.0", {"center": v(-56.52, 266.07) * mm, "radius": 9.53 * mm});
            skCircle(sketch, "E2.16.2.0", {"center": v(-56.52, 241.94) * mm, "radius": 9.53 * mm});
            skCircle(sketch, "E2.16.3.0", {"center": v(-56.52, 217.8) * mm, "radius": 9.53 * mm});
            skCircle(sketch, "E2.16.4.0", {"center": v(-56.52, 193.68) * mm, "radius": 9.53 * mm});
            skCircle(sketch, "E2.16.5.0", {"center": v(-56.52, 169.55) * mm, "radius": 9.53 * mm});
            skCircle(sketch, "E2.16.6.0", {"center": v(-56.52, 145.42) * mm, "radius": 9.53 * mm});
            skCircle(sketch, "E2.16.7.0", {"center": v(-56.52, 121.29) * mm, "radius": 9.53 * mm});
            skCircle(sketch, "E2.16.8.0", {"center": v(-56.52, 97.16) * mm, "radius": 9.53 * mm});
            skCircle(sketch, "E2.16.9.0", {"center": v(-56.52, 73.03) * mm, "radius": 9.53 * mm});
            skCircle(sketch, "E2.16.10.0", {"center": v(-56.52, 48.9) * mm, "radius": 9.53 * mm});
            skCircle(sketch, "E2.16.11.0", {"center": v(-56.52, 24.77) * mm, "radius": 9.53 * mm});
            skCircle(sketch, "E2.16.12.0", {"center": v(-56.52, 0.64) * mm, "radius": 9.53 * mm});
            skCircle(sketch, "E2.16.13.0", {"center": v(-56.52, -23.5) * mm, "radius": 9.53 * mm});
            skCircle(sketch, "E2.16.14.0", {"center": v(-56.52, -47.62) * mm, "radius": 9.53 * mm});
            skCircle(sketch, "E2.16.15.0", {"center": v(-56.52, -71.75) * mm, "radius": 9.53 * mm});
            skCircle(sketch, "E2.16.16.0", {"center": v(-56.52, -95.88) * mm, "radius": 9.53 * mm});
            skCircle(sketch, "E2.16.17.0", {"center": v(-56.52, -120.01) * mm, "radius": 9.53 * mm});
            skCircle(sketch, "E2.16.18.0", {"center": v(-56.52, -144.14) * mm, "radius": 9.53 * mm});
            skCircle(sketch, "E2.16.19.0", {"center": v(-56.52, -168.27) * mm, "radius": 9.53 * mm});
            skCircle(sketch, "E2.16.20.0", {"center": v(-56.52, -192.4) * mm, "radius": 9.53 * mm});
            skCircle(sketch, "E2.16.21.0", {"center": v(-56.52, -216.53) * mm, "radius": 9.53 * mm});
            skCircle(sketch, "E2.16.22.0", {"center": v(-56.52, -240.66) * mm, "radius": 9.53 * mm});
            skCircle(sketch, "E2.16.23.0", {"center": v(-56.52, -264.8) * mm, "radius": 9.53 * mm});
            skCircle(sketch, "E2.16.24.0", {"center": v(-56.52, -288.92) * mm, "radius": 9.53 * mm});
            skCircle(sketch, "E2.17.0.0", {"center": v(-32.39, 290.2) * mm, "radius": 9.53 * mm});
            skCircle(sketch, "E2.17.1.0", {"center": v(-32.39, 266.07) * mm, "radius": 9.53 * mm});
            skCircle(sketch, "E2.17.2.0", {"center": v(-32.39, 241.94) * mm, "radius": 9.53 * mm});
            skCircle(sketch, "E2.17.3.0", {"center": v(-32.39, 217.8) * mm, "radius": 9.53 * mm});
            skCircle(sketch, "E2.17.4.0", {"center": v(-32.39, 193.68) * mm, "radius": 9.53 * mm});
            skCircle(sketch, "E2.17.5.0", {"center": v(-32.39, 169.55) * mm, "radius": 9.53 * mm});
            skCircle(sketch, "E2.17.6.0", {"center": v(-32.39, 145.42) * mm, "radius": 9.53 * mm});
            skCircle(sketch, "E2.17.7.0", {"center": v(-32.39, 121.29) * mm, "radius": 9.53 * mm});
            skCircle(sketch, "E2.17.8.0", {"center": v(-32.39, 97.16) * mm, "radius": 9.53 * mm});
            skCircle(sketch, "E2.17.9.0", {"center": v(-32.39, 73.03) * mm, "radius": 9.53 * mm});
            skCircle(sketch, "E2.17.10.0", {"center": v(-32.39, 48.9) * mm, "radius": 9.53 * mm});
            skCircle(sketch, "E2.17.11.0", {"center": v(-32.39, 24.77) * mm, "radius": 9.53 * mm});
            skCircle(sketch, "E2.17.12.0", {"center": v(-32.39, 0.64) * mm, "radius": 9.53 * mm});
            skCircle(sketch, "E2.17.13.0", {"center": v(-32.39, -23.5) * mm, "radius": 9.53 * mm});
            skCircle(sketch, "E2.17.14.0", {"center": v(-32.39, -47.62) * mm, "radius": 9.53 * mm});
            skCircle(sketch, "E2.17.15.0", {"center": v(-32.39, -71.75) * mm, "radius": 9.53 * mm});
            skCircle(sketch, "E2.17.16.0", {"center": v(-32.39, -95.88) * mm, "radius": 9.53 * mm});
            skCircle(sketch, "E2.17.17.0", {"center": v(-32.39, -120.01) * mm, "radius": 9.53 * mm});
            skCircle(sketch, "E2.17.18.0", {"center": v(-32.39, -144.14) * mm, "radius": 9.53 * mm});
            skCircle(sketch, "E2.17.19.0", {"center": v(-32.39, -168.27) * mm, "radius": 9.53 * mm});
            skCircle(sketch, "E2.17.20.0", {"center": v(-32.39, -192.4) * mm, "radius": 9.53 * mm});
            skCircle(sketch, "E2.17.21.0", {"center": v(-32.39, -216.53) * mm, "radius": 9.53 * mm});
            skCircle(sketch, "E2.17.22.0", {"center": v(-32.39, -240.66) * mm, "radius": 9.53 * mm});
            skCircle(sketch, "E2.17.23.0", {"center": v(-32.39, -264.8) * mm, "radius": 9.53 * mm});
            skCircle(sketch, "E2.17.24.0", {"center": v(-32.39, -288.92) * mm, "radius": 9.53 * mm});
            skCircle(sketch, "E2.18.0.0", {"center": v(-8.26, 290.2) * mm, "radius": 9.53 * mm});
            skCircle(sketch, "E2.18.1.0", {"center": v(-8.26, 266.07) * mm, "radius": 9.53 * mm});
            skCircle(sketch, "E2.18.2.0", {"center": v(-8.26, 241.94) * mm, "radius": 9.53 * mm});
            skCircle(sketch, "E2.18.3.0", {"center": v(-8.26, 217.8) * mm, "radius": 9.53 * mm});
            skCircle(sketch, "E2.18.4.0", {"center": v(-8.26, 193.68) * mm, "radius": 9.53 * mm});
            skCircle(sketch, "E2.18.5.0", {"center": v(-8.26, 169.55) * mm, "radius": 9.53 * mm});
            skCircle(sketch, "E2.18.6.0", {"center": v(-8.26, 145.42) * mm, "radius": 9.53 * mm});
            skCircle(sketch, "E2.18.7.0", {"center": v(-8.26, 121.29) * mm, "radius": 9.53 * mm});
            skCircle(sketch, "E2.18.8.0", {"center": v(-8.26, 97.16) * mm, "radius": 9.53 * mm});
            skCircle(sketch, "E2.18.9.0", {"center": v(-8.26, 73.03) * mm, "radius": 9.53 * mm});
            skCircle(sketch, "E2.18.10.0", {"center": v(-8.26, 48.9) * mm, "radius": 9.53 * mm});
            skCircle(sketch, "E2.18.11.0", {"center": v(-8.26, 24.77) * mm, "radius": 9.53 * mm});
            skCircle(sketch, "E2.18.12.0", {"center": v(-8.26, 0.64) * mm, "radius": 9.53 * mm});
            skCircle(sketch, "E2.18.13.0", {"center": v(-8.26, -23.5) * mm, "radius": 9.53 * mm});
            skCircle(sketch, "E2.18.14.0", {"center": v(-8.26, -47.62) * mm, "radius": 9.53 * mm});
            skCircle(sketch, "E2.18.15.0", {"center": v(-8.26, -71.75) * mm, "radius": 9.53 * mm});
            skCircle(sketch, "E2.18.16.0", {"center": v(-8.26, -95.88) * mm, "radius": 9.53 * mm});
            skCircle(sketch, "E2.18.17.0", {"center": v(-8.26, -120.01) * mm, "radius": 9.53 * mm});
            skCircle(sketch, "E2.18.18.0", {"center": v(-8.26, -144.14) * mm, "radius": 9.53 * mm});
            skCircle(sketch, "E2.18.19.0", {"center": v(-8.26, -168.27) * mm, "radius": 9.53 * mm});
            skCircle(sketch, "E2.18.20.0", {"center": v(-8.26, -192.4) * mm, "radius": 9.53 * mm});
            skCircle(sketch, "E2.18.21.0", {"center": v(-8.26, -216.53) * mm, "radius": 9.53 * mm});
            skCircle(sketch, "E2.18.22.0", {"center": v(-8.26, -240.66) * mm, "radius": 9.53 * mm});
            skCircle(sketch, "E2.18.23.0", {"center": v(-8.26, -264.8) * mm, "radius": 9.53 * mm});
            skCircle(sketch, "E2.18.24.0", {"center": v(-8.26, -288.92) * mm, "radius": 9.53 * mm});
            skCircle(sketch, "E2.19.0.0", {"center": v(15.87, 290.2) * mm, "radius": 9.53 * mm});
            skCircle(sketch, "E2.19.1.0", {"center": v(15.87, 266.07) * mm, "radius": 9.53 * mm});
            skCircle(sketch, "E2.19.2.0", {"center": v(15.87, 241.94) * mm, "radius": 9.53 * mm});
            skCircle(sketch, "E2.19.3.0", {"center": v(15.87, 217.8) * mm, "radius": 9.53 * mm});
            skCircle(sketch, "E2.19.4.0", {"center": v(15.87, 193.68) * mm, "radius": 9.53 * mm});
            skCircle(sketch, "E2.19.5.0", {"center": v(15.87, 169.55) * mm, "radius": 9.53 * mm});
            skCircle(sketch, "E2.19.6.0", {"center": v(15.87, 145.42) * mm, "radius": 9.53 * mm});
            skCircle(sketch, "E2.19.7.0", {"center": v(15.87, 121.29) * mm, "radius": 9.53 * mm});
            skCircle(sketch, "E2.19.8.0", {"center": v(15.87, 97.16) * mm, "radius": 9.53 * mm});
            skCircle(sketch, "E2.19.9.0", {"center": v(15.87, 73.03) * mm, "radius": 9.53 * mm});
            skCircle(sketch, "E2.19.10.0", {"center": v(15.87, 48.9) * mm, "radius": 9.53 * mm});
            skCircle(sketch, "E2.19.11.0", {"center": v(15.87, 24.77) * mm, "radius": 9.53 * mm});
            skCircle(sketch, "E2.19.12.0", {"center": v(15.87, 0.64) * mm, "radius": 9.53 * mm});
            skCircle(sketch, "E2.19.13.0", {"center": v(15.87, -23.5) * mm, "radius": 9.53 * mm});
            skCircle(sketch, "E2.19.14.0", {"center": v(15.87, -47.62) * mm, "radius": 9.53 * mm});
            skCircle(sketch, "E2.19.15.0", {"center": v(15.87, -71.75) * mm, "radius": 9.53 * mm});
            skCircle(sketch, "E2.19.16.0", {"center": v(15.87, -95.88) * mm, "radius": 9.53 * mm});
            skCircle(sketch, "E2.19.17.0", {"center": v(15.87, -120.01) * mm, "radius": 9.53 * mm});
            skCircle(sketch, "E2.19.18.0", {"center": v(15.87, -144.14) * mm, "radius": 9.53 * mm});
            skCircle(sketch, "E2.19.19.0", {"center": v(15.87, -168.27) * mm, "radius": 9.53 * mm});
            skCircle(sketch, "E2.19.20.0", {"center": v(15.87, -192.4) * mm, "radius": 9.53 * mm});
            skCircle(sketch, "E2.19.21.0", {"center": v(15.87, -216.53) * mm, "radius": 9.53 * mm});
            skCircle(sketch, "E2.19.22.0", {"center": v(15.87, -240.66) * mm, "radius": 9.53 * mm});
            skCircle(sketch, "E2.19.23.0", {"center": v(15.87, -264.8) * mm, "radius": 9.53 * mm});
            skCircle(sketch, "E2.19.24.0", {"center": v(15.87, -288.92) * mm, "radius": 9.53 * mm});
            skCircle(sketch, "E2.20.0.0", {"center": v(40, 290.2) * mm, "radius": 9.53 * mm});
            skCircle(sketch, "E2.20.1.0", {"center": v(40, 266.07) * mm, "radius": 9.53 * mm});
            skCircle(sketch, "E2.20.2.0", {"center": v(40, 241.94) * mm, "radius": 9.53 * mm});
            skCircle(sketch, "E2.20.3.0", {"center": v(40, 217.8) * mm, "radius": 9.53 * mm});
            skCircle(sketch, "E2.20.4.0", {"center": v(40, 193.68) * mm, "radius": 9.53 * mm});
            skCircle(sketch, "E2.20.5.0", {"center": v(40, 169.55) * mm, "radius": 9.53 * mm});
            skCircle(sketch, "E2.20.6.0", {"center": v(40, 145.42) * mm, "radius": 9.53 * mm});
            skCircle(sketch, "E2.20.7.0", {"center": v(40, 121.29) * mm, "radius": 9.53 * mm});
            skCircle(sketch, "E2.20.8.0", {"center": v(40, 97.16) * mm, "radius": 9.53 * mm});
            skCircle(sketch, "E2.20.9.0", {"center": v(40, 73.03) * mm, "radius": 9.53 * mm});
            skCircle(sketch, "E2.20.10.0", {"center": v(40, 48.9) * mm, "radius": 9.53 * mm});
            skCircle(sketch, "E2.20.11.0", {"center": v(40, 24.77) * mm, "radius": 9.53 * mm});
            skCircle(sketch, "E2.20.12.0", {"center": v(40, 0.64) * mm, "radius": 9.53 * mm});
            skCircle(sketch, "E2.20.13.0", {"center": v(40, -23.5) * mm, "radius": 9.53 * mm});
            skCircle(sketch, "E2.20.14.0", {"center": v(40, -47.62) * mm, "radius": 9.53 * mm});
            skCircle(sketch, "E2.20.15.0", {"center": v(40, -71.75) * mm, "radius": 9.53 * mm});
            skCircle(sketch, "E2.20.16.0", {"center": v(40, -95.88) * mm, "radius": 9.53 * mm});
            skCircle(sketch, "E2.20.17.0", {"center": v(40, -120.01) * mm, "radius": 9.53 * mm});
            skCircle(sketch, "E2.20.18.0", {"center": v(40, -144.14) * mm, "radius": 9.53 * mm});
            skCircle(sketch, "E2.20.19.0", {"center": v(40, -168.27) * mm, "radius": 9.53 * mm});
            skCircle(sketch, "E2.20.20.0", {"center": v(40, -192.4) * mm, "radius": 9.53 * mm});
            skCircle(sketch, "E2.20.21.0", {"center": v(40, -216.53) * mm, "radius": 9.53 * mm});
            skCircle(sketch, "E2.20.22.0", {"center": v(40, -240.66) * mm, "radius": 9.53 * mm});
            skCircle(sketch, "E2.20.23.0", {"center": v(40, -264.8) * mm, "radius": 9.53 * mm});
            skCircle(sketch, "E2.20.24.0", {"center": v(40, -288.92) * mm, "radius": 9.53 * mm});
            skCircle(sketch, "E2.21.0.0", {"center": v(64.13, 290.2) * mm, "radius": 9.53 * mm});
            skCircle(sketch, "E2.21.1.0", {"center": v(64.13, 266.07) * mm, "radius": 9.53 * mm});
            skCircle(sketch, "E2.21.2.0", {"center": v(64.13, 241.94) * mm, "radius": 9.53 * mm});
            skCircle(sketch, "E2.21.3.0", {"center": v(64.13, 217.8) * mm, "radius": 9.53 * mm});
            skCircle(sketch, "E2.21.4.0", {"center": v(64.13, 193.68) * mm, "radius": 9.53 * mm});
            skCircle(sketch, "E2.21.5.0", {"center": v(64.13, 169.55) * mm, "radius": 9.53 * mm});
            skCircle(sketch, "E2.21.6.0", {"center": v(64.13, 145.42) * mm, "radius": 9.53 * mm});
            skCircle(sketch, "E2.21.7.0", {"center": v(64.13, 121.29) * mm, "radius": 9.53 * mm});
            skCircle(sketch, "E2.21.8.0", {"center": v(64.13, 97.16) * mm, "radius": 9.53 * mm});
            skCircle(sketch, "E2.21.9.0", {"center": v(64.13, 73.03) * mm, "radius": 9.53 * mm});
            skCircle(sketch, "E2.21.10.0", {"center": v(64.13, 48.9) * mm, "radius": 9.53 * mm});
            skCircle(sketch, "E2.21.11.0", {"center": v(64.13, 24.77) * mm, "radius": 9.53 * mm});
            skCircle(sketch, "E2.21.12.0", {"center": v(64.13, 0.64) * mm, "radius": 9.53 * mm});
            skCircle(sketch, "E2.21.13.0", {"center": v(64.13, -23.5) * mm, "radius": 9.53 * mm});
            skCircle(sketch, "E2.21.14.0", {"center": v(64.13, -47.62) * mm, "radius": 9.53 * mm});
            skCircle(sketch, "E2.21.15.0", {"center": v(64.13, -71.75) * mm, "radius": 9.53 * mm});
            skCircle(sketch, "E2.21.16.0", {"center": v(64.13, -95.88) * mm, "radius": 9.53 * mm});
            skCircle(sketch, "E2.21.17.0", {"center": v(64.13, -120.01) * mm, "radius": 9.53 * mm});
            skCircle(sketch, "E2.21.18.0", {"center": v(64.13, -144.14) * mm, "radius": 9.53 * mm});
            skCircle(sketch, "E2.21.19.0", {"center": v(64.13, -168.27) * mm, "radius": 9.53 * mm});
            skCircle(sketch, "E2.21.20.0", {"center": v(64.13, -192.4) * mm, "radius": 9.53 * mm});
            skCircle(sketch, "E2.21.21.0", {"center": v(64.13, -216.53) * mm, "radius": 9.53 * mm});
            skCircle(sketch, "E2.21.22.0", {"center": v(64.13, -240.66) * mm, "radius": 9.53 * mm});
            skCircle(sketch, "E2.21.23.0", {"center": v(64.13, -264.8) * mm, "radius": 9.53 * mm});
            skCircle(sketch, "E2.21.24.0", {"center": v(64.13, -288.92) * mm, "radius": 9.53 * mm});
            skCircle(sketch, "E2.22.0.0", {"center": v(88.26, 290.2) * mm, "radius": 9.53 * mm});
            skCircle(sketch, "E2.22.1.0", {"center": v(88.26, 266.07) * mm, "radius": 9.53 * mm});
            skCircle(sketch, "E2.22.2.0", {"center": v(88.26, 241.94) * mm, "radius": 9.53 * mm});
            skCircle(sketch, "E2.22.3.0", {"center": v(88.26, 217.8) * mm, "radius": 9.53 * mm});
            skCircle(sketch, "E2.22.4.0", {"center": v(88.26, 193.68) * mm, "radius": 9.53 * mm});
            skCircle(sketch, "E2.22.5.0", {"center": v(88.26, 169.55) * mm, "radius": 9.53 * mm});
            skCircle(sketch, "E2.22.6.0", {"center": v(88.26, 145.42) * mm, "radius": 9.53 * mm});
            skCircle(sketch, "E2.22.7.0", {"center": v(88.26, 121.29) * mm, "radius": 9.53 * mm});
            skCircle(sketch, "E2.22.8.0", {"center": v(88.26, 97.16) * mm, "radius": 9.53 * mm});
            skCircle(sketch, "E2.22.9.0", {"center": v(88.26, 73.03) * mm, "radius": 9.53 * mm});
            skCircle(sketch, "E2.22.10.0", {"center": v(88.26, 48.9) * mm, "radius": 9.53 * mm});
            skCircle(sketch, "E2.22.11.0", {"center": v(88.26, 24.77) * mm, "radius": 9.53 * mm});
            skCircle(sketch, "E2.22.12.0", {"center": v(88.26, 0.64) * mm, "radius": 9.53 * mm});
            skCircle(sketch, "E2.22.13.0", {"center": v(88.26, -23.5) * mm, "radius": 9.53 * mm});
            skCircle(sketch, "E2.22.14.0", {"center": v(88.26, -47.62) * mm, "radius": 9.53 * mm});
            skCircle(sketch, "E2.22.15.0", {"center": v(88.26, -71.75) * mm, "radius": 9.53 * mm});
            skCircle(sketch, "E2.22.16.0", {"center": v(88.26, -95.88) * mm, "radius": 9.53 * mm});
            skCircle(sketch, "E2.22.17.0", {"center": v(88.26, -120.01) * mm, "radius": 9.53 * mm});
            skCircle(sketch, "E2.22.18.0", {"center": v(88.26, -144.14) * mm, "radius": 9.53 * mm});
            skCircle(sketch, "E2.22.19.0", {"center": v(88.26, -168.27) * mm, "radius": 9.53 * mm});
            skCircle(sketch, "E2.22.20.0", {"center": v(88.26, -192.4) * mm, "radius": 9.53 * mm});
            skCircle(sketch, "E2.22.21.0", {"center": v(88.26, -216.53) * mm, "radius": 9.53 * mm});
            skCircle(sketch, "E2.22.22.0", {"center": v(88.26, -240.66) * mm, "radius": 9.53 * mm});
            skCircle(sketch, "E2.22.23.0", {"center": v(88.26, -264.8) * mm, "radius": 9.53 * mm});
            skCircle(sketch, "E2.22.24.0", {"center": v(88.26, -288.92) * mm, "radius": 9.53 * mm});
            skCircle(sketch, "E2.23.0.0", {"center": v(112.4, 290.2) * mm, "radius": 9.53 * mm});
            skCircle(sketch, "E2.23.1.0", {"center": v(112.4, 266.07) * mm, "radius": 9.53 * mm});
            skCircle(sketch, "E2.23.2.0", {"center": v(112.4, 241.94) * mm, "radius": 9.53 * mm});
            skCircle(sketch, "E2.23.3.0", {"center": v(112.4, 217.8) * mm, "radius": 9.53 * mm});
            skCircle(sketch, "E2.23.4.0", {"center": v(112.4, 193.68) * mm, "radius": 9.53 * mm});
            skCircle(sketch, "E2.23.5.0", {"center": v(112.4, 169.55) * mm, "radius": 9.53 * mm});
            skCircle(sketch, "E2.23.6.0", {"center": v(112.4, 145.42) * mm, "radius": 9.53 * mm});
            skCircle(sketch, "E2.23.7.0", {"center": v(112.4, 121.29) * mm, "radius": 9.53 * mm});
            skCircle(sketch, "E2.23.8.0", {"center": v(112.4, 97.16) * mm, "radius": 9.53 * mm});
            skCircle(sketch, "E2.23.9.0", {"center": v(112.4, 73.03) * mm, "radius": 9.53 * mm});
            skCircle(sketch, "E2.23.10.0", {"center": v(112.4, 48.9) * mm, "radius": 9.53 * mm});
            skCircle(sketch, "E2.23.11.0", {"center": v(112.4, 24.77) * mm, "radius": 9.53 * mm});
            skCircle(sketch, "E2.23.12.0", {"center": v(112.4, 0.64) * mm, "radius": 9.53 * mm});
            skCircle(sketch, "E2.23.13.0", {"center": v(112.4, -23.5) * mm, "radius": 9.53 * mm});
            skCircle(sketch, "E2.23.14.0", {"center": v(112.4, -47.62) * mm, "radius": 9.53 * mm});
            skCircle(sketch, "E2.23.15.0", {"center": v(112.4, -71.75) * mm, "radius": 9.53 * mm});
            skCircle(sketch, "E2.23.16.0", {"center": v(112.4, -95.88) * mm, "radius": 9.53 * mm});
            skCircle(sketch, "E2.23.17.0", {"center": v(112.4, -120.01) * mm, "radius": 9.53 * mm});
            skCircle(sketch, "E2.23.18.0", {"center": v(112.4, -144.14) * mm, "radius": 9.53 * mm});
            skCircle(sketch, "E2.23.19.0", {"center": v(112.4, -168.27) * mm, "radius": 9.53 * mm});
            skCircle(sketch, "E2.23.20.0", {"center": v(112.4, -192.4) * mm, "radius": 9.53 * mm});
            skCircle(sketch, "E2.23.21.0", {"center": v(112.4, -216.53) * mm, "radius": 9.53 * mm});
            skCircle(sketch, "E2.23.22.0", {"center": v(112.4, -240.66) * mm, "radius": 9.53 * mm});
            skCircle(sketch, "E2.23.23.0", {"center": v(112.4, -264.8) * mm, "radius": 9.53 * mm});
            skCircle(sketch, "E2.23.24.0", {"center": v(112.4, -288.92) * mm, "radius": 9.53 * mm});
            skCircle(sketch, "E2.24.0.0", {"center": v(136.52, 290.2) * mm, "radius": 9.53 * mm});
            skCircle(sketch, "E2.24.1.0", {"center": v(136.52, 266.07) * mm, "radius": 9.53 * mm});
            skCircle(sketch, "E2.24.2.0", {"center": v(136.52, 241.94) * mm, "radius": 9.53 * mm});
            skCircle(sketch, "E2.24.3.0", {"center": v(136.52, 217.8) * mm, "radius": 9.53 * mm});
            skCircle(sketch, "E2.24.4.0", {"center": v(136.52, 193.68) * mm, "radius": 9.53 * mm});
            skCircle(sketch, "E2.24.5.0", {"center": v(136.52, 169.55) * mm, "radius": 9.53 * mm});
            skCircle(sketch, "E2.24.6.0", {"center": v(136.52, 145.42) * mm, "radius": 9.53 * mm});
            skCircle(sketch, "E2.24.7.0", {"center": v(136.52, 121.29) * mm, "radius": 9.53 * mm});
            skCircle(sketch, "E2.24.8.0", {"center": v(136.52, 97.16) * mm, "radius": 9.53 * mm});
            skCircle(sketch, "E2.24.9.0", {"center": v(136.52, 73.03) * mm, "radius": 9.53 * mm});
            skCircle(sketch, "E2.24.10.0", {"center": v(136.52, 48.9) * mm, "radius": 9.53 * mm});
            skCircle(sketch, "E2.24.11.0", {"center": v(136.52, 24.77) * mm, "radius": 9.53 * mm});
            skCircle(sketch, "E2.24.12.0", {"center": v(136.52, 0.64) * mm, "radius": 9.53 * mm});
            skCircle(sketch, "E2.24.13.0", {"center": v(136.52, -23.5) * mm, "radius": 9.53 * mm});
            skCircle(sketch, "E2.24.14.0", {"center": v(136.52, -47.62) * mm, "radius": 9.53 * mm});
            skCircle(sketch, "E2.24.15.0", {"center": v(136.52, -71.75) * mm, "radius": 9.53 * mm});
            skCircle(sketch, "E2.24.16.0", {"center": v(136.52, -95.88) * mm, "radius": 9.53 * mm});
            skCircle(sketch, "E2.24.17.0", {"center": v(136.52, -120.01) * mm, "radius": 9.53 * mm});
            skCircle(sketch, "E2.24.18.0", {"center": v(136.52, -144.14) * mm, "radius": 9.53 * mm});
            skCircle(sketch, "E2.24.19.0", {"center": v(136.52, -168.27) * mm, "radius": 9.53 * mm});
            skCircle(sketch, "E2.24.20.0", {"center": v(136.52, -192.4) * mm, "radius": 9.53 * mm});
            skCircle(sketch, "E2.24.21.0", {"center": v(136.52, -216.53) * mm, "radius": 9.53 * mm});
            skCircle(sketch, "E2.24.22.0", {"center": v(136.52, -240.66) * mm, "radius": 9.53 * mm});
            skCircle(sketch, "E2.24.23.0", {"center": v(136.52, -264.8) * mm, "radius": 9.53 * mm});
            skCircle(sketch, "E2.24.24.0", {"center": v(136.52, -288.92) * mm, "radius": 9.53 * mm});
            skCircle(sketch, "E2.25.0.0", {"center": v(160.65, 290.2) * mm, "radius": 9.53 * mm});
            skCircle(sketch, "E2.25.1.0", {"center": v(160.65, 266.07) * mm, "radius": 9.53 * mm});
            skCircle(sketch, "E2.25.2.0", {"center": v(160.65, 241.94) * mm, "radius": 9.53 * mm});
            skCircle(sketch, "E2.25.3.0", {"center": v(160.65, 217.8) * mm, "radius": 9.53 * mm});
            skCircle(sketch, "E2.25.4.0", {"center": v(160.65, 193.68) * mm, "radius": 9.53 * mm});
            skCircle(sketch, "E2.25.5.0", {"center": v(160.65, 169.55) * mm, "radius": 9.53 * mm});
            skCircle(sketch, "E2.25.6.0", {"center": v(160.65, 145.42) * mm, "radius": 9.53 * mm});
            skCircle(sketch, "E2.25.7.0", {"center": v(160.65, 121.29) * mm, "radius": 9.53 * mm});
            skCircle(sketch, "E2.25.8.0", {"center": v(160.65, 97.16) * mm, "radius": 9.53 * mm});
            skCircle(sketch, "E2.25.9.0", {"center": v(160.65, 73.03) * mm, "radius": 9.53 * mm});
            skCircle(sketch, "E2.25.10.0", {"center": v(160.65, 48.9) * mm, "radius": 9.53 * mm});
            skCircle(sketch, "E2.25.11.0", {"center": v(160.65, 24.77) * mm, "radius": 9.53 * mm});
            skCircle(sketch, "E2.25.12.0", {"center": v(160.65, 0.64) * mm, "radius": 9.53 * mm});
            skCircle(sketch, "E2.25.13.0", {"center": v(160.65, -23.5) * mm, "radius": 9.53 * mm});
            skCircle(sketch, "E2.25.14.0", {"center": v(160.65, -47.62) * mm, "radius": 9.53 * mm});
            skCircle(sketch, "E2.25.15.0", {"center": v(160.65, -71.75) * mm, "radius": 9.53 * mm});
            skCircle(sketch, "E2.25.16.0", {"center": v(160.65, -95.88) * mm, "radius": 9.53 * mm});
            skCircle(sketch, "E2.25.17.0", {"center": v(160.65, -120.01) * mm, "radius": 9.53 * mm});
            skCircle(sketch, "E2.25.18.0", {"center": v(160.65, -144.14) * mm, "radius": 9.53 * mm});
            skCircle(sketch, "E2.25.19.0", {"center": v(160.65, -168.27) * mm, "radius": 9.53 * mm});
            skCircle(sketch, "E2.25.20.0", {"center": v(160.65, -192.4) * mm, "radius": 9.53 * mm});
            skCircle(sketch, "E2.25.21.0", {"center": v(160.65, -216.53) * mm, "radius": 9.53 * mm});
            skCircle(sketch, "E2.25.22.0", {"center": v(160.65, -240.66) * mm, "radius": 9.53 * mm});
            skCircle(sketch, "E2.25.23.0", {"center": v(160.65, -264.8) * mm, "radius": 9.53 * mm});
            skCircle(sketch, "E2.25.24.0", {"center": v(160.65, -288.92) * mm, "radius": 9.53 * mm});
            skCircle(sketch, "E2.26.0.0", {"center": v(184.78, 290.2) * mm, "radius": 9.53 * mm});
            skCircle(sketch, "E2.26.1.0", {"center": v(184.78, 266.07) * mm, "radius": 9.53 * mm});
            skCircle(sketch, "E2.26.2.0", {"center": v(184.78, 241.94) * mm, "radius": 9.53 * mm});
            skCircle(sketch, "E2.26.3.0", {"center": v(184.78, 217.8) * mm, "radius": 9.53 * mm});
            skCircle(sketch, "E2.26.4.0", {"center": v(184.78, 193.68) * mm, "radius": 9.53 * mm});
            skCircle(sketch, "E2.26.5.0", {"center": v(184.78, 169.55) * mm, "radius": 9.53 * mm});
            skCircle(sketch, "E2.26.6.0", {"center": v(184.78, 145.42) * mm, "radius": 9.53 * mm});
            skCircle(sketch, "E2.26.7.0", {"center": v(184.78, 121.29) * mm, "radius": 9.53 * mm});
            skCircle(sketch, "E2.26.8.0", {"center": v(184.78, 97.16) * mm, "radius": 9.53 * mm});
            skCircle(sketch, "E2.26.9.0", {"center": v(184.78, 73.03) * mm, "radius": 9.53 * mm});
            skCircle(sketch, "E2.26.10.0", {"center": v(184.78, 48.9) * mm, "radius": 9.53 * mm});
            skCircle(sketch, "E2.26.11.0", {"center": v(184.78, 24.77) * mm, "radius": 9.53 * mm});
            skCircle(sketch, "E2.26.12.0", {"center": v(184.78, 0.64) * mm, "radius": 9.53 * mm});
            skCircle(sketch, "E2.26.13.0", {"center": v(184.78, -23.5) * mm, "radius": 9.53 * mm});
            skCircle(sketch, "E2.26.14.0", {"center": v(184.78, -47.62) * mm, "radius": 9.53 * mm});
            skCircle(sketch, "E2.26.15.0", {"center": v(184.78, -71.75) * mm, "radius": 9.53 * mm});
            skCircle(sketch, "E2.26.16.0", {"center": v(184.78, -95.88) * mm, "radius": 9.53 * mm});
            skCircle(sketch, "E2.26.17.0", {"center": v(184.78, -120.01) * mm, "radius": 9.53 * mm});
            skCircle(sketch, "E2.26.18.0", {"center": v(184.78, -144.14) * mm, "radius": 9.53 * mm});
            skCircle(sketch, "E2.26.19.0", {"center": v(184.78, -168.27) * mm, "radius": 9.53 * mm});
            skCircle(sketch, "E2.26.20.0", {"center": v(184.78, -192.4) * mm, "radius": 9.53 * mm});
            skCircle(sketch, "E2.26.21.0", {"center": v(184.78, -216.53) * mm, "radius": 9.53 * mm});
            skCircle(sketch, "E2.26.22.0", {"center": v(184.78, -240.66) * mm, "radius": 9.53 * mm});
            skCircle(sketch, "E2.26.23.0", {"center": v(184.78, -264.8) * mm, "radius": 9.53 * mm});
            skCircle(sketch, "E2.26.24.0", {"center": v(184.78, -288.92) * mm, "radius": 9.53 * mm});
            skCircle(sketch, "E2.27.0.0", {"center": v(208.91, 290.2) * mm, "radius": 9.53 * mm});
            skCircle(sketch, "E2.27.1.0", {"center": v(208.91, 266.07) * mm, "radius": 9.53 * mm});
            skCircle(sketch, "E2.27.2.0", {"center": v(208.91, 241.94) * mm, "radius": 9.53 * mm});
            skCircle(sketch, "E2.27.3.0", {"center": v(208.91, 217.8) * mm, "radius": 9.53 * mm});
            skCircle(sketch, "E2.27.4.0", {"center": v(208.91, 193.68) * mm, "radius": 9.53 * mm});
            skCircle(sketch, "E2.27.5.0", {"center": v(208.91, 169.55) * mm, "radius": 9.53 * mm});
            skCircle(sketch, "E2.27.6.0", {"center": v(208.91, 145.42) * mm, "radius": 9.53 * mm});
            skCircle(sketch, "E2.27.7.0", {"center": v(208.91, 121.29) * mm, "radius": 9.53 * mm});
            skCircle(sketch, "E2.27.8.0", {"center": v(208.91, 97.16) * mm, "radius": 9.53 * mm});
            skCircle(sketch, "E2.27.9.0", {"center": v(208.91, 73.03) * mm, "radius": 9.53 * mm});
            skCircle(sketch, "E2.27.10.0", {"center": v(208.91, 48.9) * mm, "radius": 9.53 * mm});
            skCircle(sketch, "E2.27.11.0", {"center": v(208.91, 24.77) * mm, "radius": 9.53 * mm});
            skCircle(sketch, "E2.27.12.0", {"center": v(208.91, 0.64) * mm, "radius": 9.53 * mm});
            skCircle(sketch, "E2.27.13.0", {"center": v(208.91, -23.5) * mm, "radius": 9.53 * mm});
            skCircle(sketch, "E2.27.14.0", {"center": v(208.91, -47.62) * mm, "radius": 9.53 * mm});
            skCircle(sketch, "E2.27.15.0", {"center": v(208.91, -71.75) * mm, "radius": 9.53 * mm});
            skCircle(sketch, "E2.27.16.0", {"center": v(208.91, -95.88) * mm, "radius": 9.53 * mm});
            skCircle(sketch, "E2.27.17.0", {"center": v(208.91, -120.01) * mm, "radius": 9.53 * mm});
            skCircle(sketch, "E2.27.18.0", {"center": v(208.91, -144.14) * mm, "radius": 9.53 * mm});
            skCircle(sketch, "E2.27.19.0", {"center": v(208.91, -168.27) * mm, "radius": 9.53 * mm});
            skCircle(sketch, "E2.27.20.0", {"center": v(208.91, -192.4) * mm, "radius": 9.53 * mm});
            skCircle(sketch, "E2.27.21.0", {"center": v(208.91, -216.53) * mm, "radius": 9.53 * mm});
            skCircle(sketch, "E2.27.22.0", {"center": v(208.91, -240.66) * mm, "radius": 9.53 * mm});
            skCircle(sketch, "E2.27.23.0", {"center": v(208.91, -264.8) * mm, "radius": 9.53 * mm});
            skCircle(sketch, "E2.27.24.0", {"center": v(208.91, -288.92) * mm, "radius": 9.53 * mm});
            skCircle(sketch, "E2.28.0.0", {"center": v(233.04, 290.2) * mm, "radius": 9.53 * mm});
            skCircle(sketch, "E2.28.1.0", {"center": v(233.04, 266.07) * mm, "radius": 9.53 * mm});
            skCircle(sketch, "E2.28.2.0", {"center": v(233.04, 241.94) * mm, "radius": 9.53 * mm});
            skCircle(sketch, "E2.28.3.0", {"center": v(233.04, 217.8) * mm, "radius": 9.53 * mm});
            skCircle(sketch, "E2.28.4.0", {"center": v(233.04, 193.68) * mm, "radius": 9.53 * mm});
            skCircle(sketch, "E2.28.5.0", {"center": v(233.04, 169.55) * mm, "radius": 9.53 * mm});
            skCircle(sketch, "E2.28.6.0", {"center": v(233.04, 145.42) * mm, "radius": 9.53 * mm});
            skCircle(sketch, "E2.28.7.0", {"center": v(233.04, 121.29) * mm, "radius": 9.53 * mm});
            skCircle(sketch, "E2.28.8.0", {"center": v(233.04, 97.16) * mm, "radius": 9.53 * mm});
            skCircle(sketch, "E2.28.9.0", {"center": v(233.04, 73.03) * mm, "radius": 9.53 * mm});
            skCircle(sketch, "E2.28.10.0", {"center": v(233.04, 48.9) * mm, "radius": 9.53 * mm});
            skCircle(sketch, "E2.28.11.0", {"center": v(233.04, 24.77) * mm, "radius": 9.53 * mm});
            skCircle(sketch, "E2.28.12.0", {"center": v(233.04, 0.64) * mm, "radius": 9.53 * mm});
            skCircle(sketch, "E2.28.13.0", {"center": v(233.04, -23.5) * mm, "radius": 9.53 * mm});
            skCircle(sketch, "E2.28.14.0", {"center": v(233.04, -47.62) * mm, "radius": 9.53 * mm});
            skCircle(sketch, "E2.28.15.0", {"center": v(233.04, -71.75) * mm, "radius": 9.53 * mm});
            skCircle(sketch, "E2.28.16.0", {"center": v(233.04, -95.88) * mm, "radius": 9.53 * mm});
            skCircle(sketch, "E2.28.17.0", {"center": v(233.04, -120.01) * mm, "radius": 9.53 * mm});
            skCircle(sketch, "E2.28.18.0", {"center": v(233.04, -144.14) * mm, "radius": 9.53 * mm});
            skCircle(sketch, "E2.28.19.0", {"center": v(233.04, -168.27) * mm, "radius": 9.53 * mm});
            skCircle(sketch, "E2.28.20.0", {"center": v(233.04, -192.4) * mm, "radius": 9.53 * mm});
            skCircle(sketch, "E2.28.21.0", {"center": v(233.04, -216.53) * mm, "radius": 9.53 * mm});
            skCircle(sketch, "E2.28.22.0", {"center": v(233.04, -240.66) * mm, "radius": 9.53 * mm});
            skCircle(sketch, "E2.28.23.0", {"center": v(233.04, -264.8) * mm, "radius": 9.53 * mm});
            skCircle(sketch, "E2.28.24.0", {"center": v(233.04, -288.92) * mm, "radius": 9.53 * mm});
            skCircle(sketch, "E2.29.0.0", {"center": v(257.17, 290.2) * mm, "radius": 9.53 * mm});
            skCircle(sketch, "E2.29.1.0", {"center": v(257.17, 266.07) * mm, "radius": 9.53 * mm});
            skCircle(sketch, "E2.29.2.0", {"center": v(257.17, 241.94) * mm, "radius": 9.53 * mm});
            skCircle(sketch, "E2.29.3.0", {"center": v(257.17, 217.8) * mm, "radius": 9.53 * mm});
            skCircle(sketch, "E2.29.4.0", {"center": v(257.17, 193.68) * mm, "radius": 9.53 * mm});
            skCircle(sketch, "E2.29.5.0", {"center": v(257.17, 169.55) * mm, "radius": 9.53 * mm});
            skCircle(sketch, "E2.29.6.0", {"center": v(257.17, 145.42) * mm, "radius": 9.53 * mm});
            skCircle(sketch, "E2.29.7.0", {"center": v(257.17, 121.29) * mm, "radius": 9.53 * mm});
            skCircle(sketch, "E2.29.8.0", {"center": v(257.17, 97.16) * mm, "radius": 9.53 * mm});
            skCircle(sketch, "E2.29.9.0", {"center": v(257.17, 73.03) * mm, "radius": 9.53 * mm});
            skCircle(sketch, "E2.29.10.0", {"center": v(257.17, 48.9) * mm, "radius": 9.53 * mm});
            skCircle(sketch, "E2.29.11.0", {"center": v(257.17, 24.77) * mm, "radius": 9.53 * mm});
            skCircle(sketch, "E2.29.12.0", {"center": v(257.17, 0.64) * mm, "radius": 9.53 * mm});
            skCircle(sketch, "E2.29.13.0", {"center": v(257.17, -23.5) * mm, "radius": 9.53 * mm});
            skCircle(sketch, "E2.29.14.0", {"center": v(257.17, -47.62) * mm, "radius": 9.53 * mm});
            skCircle(sketch, "E2.29.15.0", {"center": v(257.17, -71.75) * mm, "radius": 9.53 * mm});
            skCircle(sketch, "E2.29.16.0", {"center": v(257.17, -95.88) * mm, "radius": 9.53 * mm});
            skCircle(sketch, "E2.29.17.0", {"center": v(257.17, -120.01) * mm, "radius": 9.53 * mm});
            skCircle(sketch, "E2.29.18.0", {"center": v(257.17, -144.14) * mm, "radius": 9.53 * mm});
            skCircle(sketch, "E2.29.19.0", {"center": v(257.17, -168.27) * mm, "radius": 9.53 * mm});
            skCircle(sketch, "E2.29.20.0", {"center": v(257.17, -192.4) * mm, "radius": 9.53 * mm});
            skCircle(sketch, "E2.29.21.0", {"center": v(257.17, -216.53) * mm, "radius": 9.53 * mm});
            skCircle(sketch, "E2.29.22.0", {"center": v(257.17, -240.66) * mm, "radius": 9.53 * mm});
            skCircle(sketch, "E2.29.23.0", {"center": v(257.17, -264.8) * mm, "radius": 9.53 * mm});
            skCircle(sketch, "E2.29.24.0", {"center": v(257.17, -288.92) * mm, "radius": 9.53 * mm});
            skCircle(sketch, "E2.30.0.0", {"center": v(281.3, 290.2) * mm, "radius": 9.53 * mm});
            skCircle(sketch, "E2.30.1.0", {"center": v(281.3, 266.07) * mm, "radius": 9.53 * mm});
            skCircle(sketch, "E2.30.2.0", {"center": v(281.3, 241.94) * mm, "radius": 9.53 * mm});
            skCircle(sketch, "E2.30.3.0", {"center": v(281.3, 217.8) * mm, "radius": 9.53 * mm});
            skCircle(sketch, "E2.30.4.0", {"center": v(281.3, 193.68) * mm, "radius": 9.53 * mm});
            skCircle(sketch, "E2.30.5.0", {"center": v(281.3, 169.55) * mm, "radius": 9.53 * mm});
            skCircle(sketch, "E2.30.6.0", {"center": v(281.3, 145.42) * mm, "radius": 9.53 * mm});
            skCircle(sketch, "E2.30.7.0", {"center": v(281.3, 121.29) * mm, "radius": 9.53 * mm});
            skCircle(sketch, "E2.30.8.0", {"center": v(281.3, 97.16) * mm, "radius": 9.53 * mm});
            skCircle(sketch, "E2.30.9.0", {"center": v(281.3, 73.03) * mm, "radius": 9.53 * mm});
            skCircle(sketch, "E2.30.10.0", {"center": v(281.3, 48.9) * mm, "radius": 9.53 * mm});
            skCircle(sketch, "E2.30.11.0", {"center": v(281.3, 24.77) * mm, "radius": 9.53 * mm});
            skCircle(sketch, "E2.30.12.0", {"center": v(281.3, 0.64) * mm, "radius": 9.53 * mm});
            skCircle(sketch, "E2.30.13.0", {"center": v(281.3, -23.5) * mm, "radius": 9.53 * mm});
            skCircle(sketch, "E2.30.14.0", {"center": v(281.3, -47.62) * mm, "radius": 9.53 * mm});
            skCircle(sketch, "E2.30.15.0", {"center": v(281.3, -71.75) * mm, "radius": 9.53 * mm});
            skCircle(sketch, "E2.30.16.0", {"center": v(281.3, -95.88) * mm, "radius": 9.53 * mm});
            skCircle(sketch, "E2.30.17.0", {"center": v(281.3, -120.01) * mm, "radius": 9.53 * mm});
            skCircle(sketch, "E2.30.18.0", {"center": v(281.3, -144.14) * mm, "radius": 9.53 * mm});
            skCircle(sketch, "E2.30.19.0", {"center": v(281.3, -168.27) * mm, "radius": 9.53 * mm});
            skCircle(sketch, "E2.30.20.0", {"center": v(281.3, -192.4) * mm, "radius": 9.53 * mm});
            skCircle(sketch, "E2.30.21.0", {"center": v(281.3, -216.53) * mm, "radius": 9.53 * mm});
            skCircle(sketch, "E2.30.22.0", {"center": v(281.3, -240.66) * mm, "radius": 9.53 * mm});
            skCircle(sketch, "E2.30.23.0", {"center": v(281.3, -264.8) * mm, "radius": 9.53 * mm});
            skCircle(sketch, "E2.30.24.0", {"center": v(281.3, -288.92) * mm, "radius": 9.53 * mm});
            skCircle(sketch, "E2.31.0.0", {"center": v(305.43, 290.2) * mm, "radius": 9.53 * mm});
            skCircle(sketch, "E2.31.1.0", {"center": v(305.43, 266.07) * mm, "radius": 9.53 * mm});
            skCircle(sketch, "E2.31.2.0", {"center": v(305.43, 241.94) * mm, "radius": 9.53 * mm});
            skCircle(sketch, "E2.31.3.0", {"center": v(305.43, 217.8) * mm, "radius": 9.53 * mm});
            skCircle(sketch, "E2.31.4.0", {"center": v(305.43, 193.68) * mm, "radius": 9.53 * mm});
            skCircle(sketch, "E2.31.5.0", {"center": v(305.43, 169.55) * mm, "radius": 9.53 * mm});
            skCircle(sketch, "E2.31.6.0", {"center": v(305.43, 145.42) * mm, "radius": 9.53 * mm});
            skCircle(sketch, "E2.31.7.0", {"center": v(305.43, 121.29) * mm, "radius": 9.53 * mm});
            skCircle(sketch, "E2.31.8.0", {"center": v(305.43, 97.16) * mm, "radius": 9.53 * mm});
            skCircle(sketch, "E2.31.9.0", {"center": v(305.43, 73.03) * mm, "radius": 9.53 * mm});
            skCircle(sketch, "E2.31.10.0", {"center": v(305.43, 48.9) * mm, "radius": 9.53 * mm});
            skCircle(sketch, "E2.31.11.0", {"center": v(305.43, 24.77) * mm, "radius": 9.53 * mm});
            skCircle(sketch, "E2.31.12.0", {"center": v(305.43, 0.64) * mm, "radius": 9.53 * mm});
            skCircle(sketch, "E2.31.13.0", {"center": v(305.43, -23.5) * mm, "radius": 9.53 * mm});
            skCircle(sketch, "E2.31.14.0", {"center": v(305.43, -47.62) * mm, "radius": 9.53 * mm});
            skCircle(sketch, "E2.31.15.0", {"center": v(305.43, -71.75) * mm, "radius": 9.53 * mm});
            skCircle(sketch, "E2.31.16.0", {"center": v(305.43, -95.88) * mm, "radius": 9.53 * mm});
            skCircle(sketch, "E2.31.17.0", {"center": v(305.43, -120.01) * mm, "radius": 9.53 * mm});
            skCircle(sketch, "E2.31.18.0", {"center": v(305.43, -144.14) * mm, "radius": 9.53 * mm});
            skCircle(sketch, "E2.31.19.0", {"center": v(305.43, -168.27) * mm, "radius": 9.53 * mm});
            skCircle(sketch, "E2.31.20.0", {"center": v(305.43, -192.4) * mm, "radius": 9.53 * mm});
            skCircle(sketch, "E2.31.21.0", {"center": v(305.43, -216.53) * mm, "radius": 9.53 * mm});
            skCircle(sketch, "E2.31.22.0", {"center": v(305.43, -240.66) * mm, "radius": 9.53 * mm});
            skCircle(sketch, "E2.31.23.0", {"center": v(305.43, -264.8) * mm, "radius": 9.53 * mm});
            skCircle(sketch, "E2.31.24.0", {"center": v(305.43, -288.92) * mm, "radius": 9.53 * mm});
            skCircle(sketch, "E2.32.0.0", {"center": v(329.56, 290.2) * mm, "radius": 9.53 * mm});
            skCircle(sketch, "E2.32.1.0", {"center": v(329.56, 266.07) * mm, "radius": 9.53 * mm});
            skCircle(sketch, "E2.32.2.0", {"center": v(329.56, 241.94) * mm, "radius": 9.53 * mm});
            skCircle(sketch, "E2.32.3.0", {"center": v(329.56, 217.8) * mm, "radius": 9.53 * mm});
            skCircle(sketch, "E2.32.4.0", {"center": v(329.56, 193.68) * mm, "radius": 9.53 * mm});
            skCircle(sketch, "E2.32.5.0", {"center": v(329.56, 169.55) * mm, "radius": 9.53 * mm});
            skCircle(sketch, "E2.32.6.0", {"center": v(329.56, 145.42) * mm, "radius": 9.53 * mm});
            skCircle(sketch, "E2.32.7.0", {"center": v(329.56, 121.29) * mm, "radius": 9.53 * mm});
            skCircle(sketch, "E2.32.8.0", {"center": v(329.56, 97.16) * mm, "radius": 9.53 * mm});
            skCircle(sketch, "E2.32.9.0", {"center": v(329.56, 73.03) * mm, "radius": 9.53 * mm});
            skCircle(sketch, "E2.32.10.0", {"center": v(329.56, 48.9) * mm, "radius": 9.53 * mm});
            skCircle(sketch, "E2.32.11.0", {"center": v(329.56, 24.77) * mm, "radius": 9.53 * mm});
            skCircle(sketch, "E2.32.12.0", {"center": v(329.56, 0.64) * mm, "radius": 9.53 * mm});
            skCircle(sketch, "E2.32.13.0", {"center": v(329.56, -23.5) * mm, "radius": 9.53 * mm});
            skCircle(sketch, "E2.32.14.0", {"center": v(329.56, -47.62) * mm, "radius": 9.53 * mm});
            skCircle(sketch, "E2.32.15.0", {"center": v(329.56, -71.75) * mm, "radius": 9.53 * mm});
            skCircle(sketch, "E2.32.16.0", {"center": v(329.56, -95.88) * mm, "radius": 9.53 * mm});
            skCircle(sketch, "E2.32.17.0", {"center": v(329.56, -120.01) * mm, "radius": 9.53 * mm});
            skCircle(sketch, "E2.32.18.0", {"center": v(329.56, -144.14) * mm, "radius": 9.53 * mm});
            skCircle(sketch, "E2.32.19.0", {"center": v(329.56, -168.27) * mm, "radius": 9.53 * mm});
            skCircle(sketch, "E2.32.20.0", {"center": v(329.56, -192.4) * mm, "radius": 9.53 * mm});
            skCircle(sketch, "E2.32.21.0", {"center": v(329.56, -216.53) * mm, "radius": 9.53 * mm});
            skCircle(sketch, "E2.32.22.0", {"center": v(329.56, -240.66) * mm, "radius": 9.53 * mm});
            skCircle(sketch, "E2.32.23.0", {"center": v(329.56, -264.8) * mm, "radius": 9.53 * mm});
            skCircle(sketch, "E2.32.24.0", {"center": v(329.56, -288.92) * mm, "radius": 9.53 * mm});
            skCircle(sketch, "E2.33.0.0", {"center": v(353.7, 290.2) * mm, "radius": 9.53 * mm});
            skCircle(sketch, "E2.33.1.0", {"center": v(353.7, 266.07) * mm, "radius": 9.53 * mm});
            skCircle(sketch, "E2.33.2.0", {"center": v(353.7, 241.94) * mm, "radius": 9.53 * mm});
            skCircle(sketch, "E2.33.3.0", {"center": v(353.7, 217.8) * mm, "radius": 9.53 * mm});
            skCircle(sketch, "E2.33.4.0", {"center": v(353.7, 193.68) * mm, "radius": 9.53 * mm});
            skCircle(sketch, "E2.33.5.0", {"center": v(353.7, 169.55) * mm, "radius": 9.53 * mm});
            skCircle(sketch, "E2.33.6.0", {"center": v(353.7, 145.42) * mm, "radius": 9.53 * mm});
            skCircle(sketch, "E2.33.7.0", {"center": v(353.7, 121.29) * mm, "radius": 9.53 * mm});
            skCircle(sketch, "E2.33.8.0", {"center": v(353.7, 97.16) * mm, "radius": 9.53 * mm});
            skCircle(sketch, "E2.33.9.0", {"center": v(353.7, 73.03) * mm, "radius": 9.53 * mm});
            skCircle(sketch, "E2.33.10.0", {"center": v(353.7, 48.9) * mm, "radius": 9.53 * mm});
            skCircle(sketch, "E2.33.11.0", {"center": v(353.7, 24.77) * mm, "radius": 9.53 * mm});
            skCircle(sketch, "E2.33.12.0", {"center": v(353.7, 0.64) * mm, "radius": 9.53 * mm});
            skCircle(sketch, "E2.33.13.0", {"center": v(353.7, -23.5) * mm, "radius": 9.53 * mm});
            skCircle(sketch, "E2.33.14.0", {"center": v(353.7, -47.62) * mm, "radius": 9.53 * mm});
            skCircle(sketch, "E2.33.15.0", {"center": v(353.7, -71.75) * mm, "radius": 9.53 * mm});
            skCircle(sketch, "E2.33.16.0", {"center": v(353.7, -95.88) * mm, "radius": 9.53 * mm});
            skCircle(sketch, "E2.33.17.0", {"center": v(353.7, -120.01) * mm, "radius": 9.53 * mm});
            skCircle(sketch, "E2.33.18.0", {"center": v(353.7, -144.14) * mm, "radius": 9.53 * mm});
            skCircle(sketch, "E2.33.19.0", {"center": v(353.7, -168.27) * mm, "radius": 9.53 * mm});
            skCircle(sketch, "E2.33.20.0", {"center": v(353.7, -192.4) * mm, "radius": 9.53 * mm});
            skCircle(sketch, "E2.33.21.0", {"center": v(353.7, -216.53) * mm, "radius": 9.53 * mm});
            skCircle(sketch, "E2.33.22.0", {"center": v(353.7, -240.66) * mm, "radius": 9.53 * mm});
            skCircle(sketch, "E2.33.23.0", {"center": v(353.7, -264.8) * mm, "radius": 9.53 * mm});
            skCircle(sketch, "E2.33.24.0", {"center": v(353.7, -288.92) * mm, "radius": 9.53 * mm});
            skCircle(sketch, "E2.34.0.0", {"center": v(377.82, 290.2) * mm, "radius": 9.53 * mm});
            skCircle(sketch, "E2.34.1.0", {"center": v(377.82, 266.07) * mm, "radius": 9.53 * mm});
            skCircle(sketch, "E2.34.2.0", {"center": v(377.82, 241.94) * mm, "radius": 9.53 * mm});
            skCircle(sketch, "E2.34.3.0", {"center": v(377.82, 217.8) * mm, "radius": 9.53 * mm});
            skCircle(sketch, "E2.34.4.0", {"center": v(377.82, 193.68) * mm, "radius": 9.53 * mm});
            skCircle(sketch, "E2.34.5.0", {"center": v(377.82, 169.55) * mm, "radius": 9.53 * mm});
            skCircle(sketch, "E2.34.6.0", {"center": v(377.82, 145.42) * mm, "radius": 9.53 * mm});
            skCircle(sketch, "E2.34.7.0", {"center": v(377.82, 121.29) * mm, "radius": 9.53 * mm});
            skCircle(sketch, "E2.34.8.0", {"center": v(377.82, 97.16) * mm, "radius": 9.53 * mm});
            skCircle(sketch, "E2.34.9.0", {"center": v(377.82, 73.03) * mm, "radius": 9.53 * mm});
            skCircle(sketch, "E2.34.10.0", {"center": v(377.82, 48.9) * mm, "radius": 9.53 * mm});
            skCircle(sketch, "E2.34.11.0", {"center": v(377.82, 24.77) * mm, "radius": 9.53 * mm});
            skCircle(sketch, "E2.34.12.0", {"center": v(377.82, 0.64) * mm, "radius": 9.53 * mm});
            skCircle(sketch, "E2.34.13.0", {"center": v(377.82, -23.5) * mm, "radius": 9.53 * mm});
            skCircle(sketch, "E2.34.14.0", {"center": v(377.82, -47.62) * mm, "radius": 9.53 * mm});
            skCircle(sketch, "E2.34.15.0", {"center": v(377.82, -71.75) * mm, "radius": 9.53 * mm});
            skCircle(sketch, "E2.34.16.0", {"center": v(377.82, -95.88) * mm, "radius": 9.53 * mm});
            skCircle(sketch, "E2.34.17.0", {"center": v(377.82, -120.01) * mm, "radius": 9.53 * mm});
            skCircle(sketch, "E2.34.18.0", {"center": v(377.82, -144.14) * mm, "radius": 9.53 * mm});
            skCircle(sketch, "E2.34.19.0", {"center": v(377.82, -168.27) * mm, "radius": 9.53 * mm});
            skCircle(sketch, "E2.34.20.0", {"center": v(377.82, -192.4) * mm, "radius": 9.53 * mm});
            skCircle(sketch, "E2.34.21.0", {"center": v(377.82, -216.53) * mm, "radius": 9.53 * mm});
            skCircle(sketch, "E2.34.22.0", {"center": v(377.82, -240.66) * mm, "radius": 9.53 * mm});
            skCircle(sketch, "E2.34.23.0", {"center": v(377.82, -264.8) * mm, "radius": 9.53 * mm});
            skCircle(sketch, "E2.34.24.0", {"center": v(377.82, -288.92) * mm, "radius": 9.53 * mm});
            skCircle(sketch, "E2.35.0.0", {"center": v(401.95, 290.2) * mm, "radius": 9.53 * mm});
            skCircle(sketch, "E2.35.1.0", {"center": v(401.95, 266.07) * mm, "radius": 9.53 * mm});
            skCircle(sketch, "E2.35.2.0", {"center": v(401.95, 241.94) * mm, "radius": 9.53 * mm});
            skCircle(sketch, "E2.35.3.0", {"center": v(401.95, 217.8) * mm, "radius": 9.53 * mm});
            skCircle(sketch, "E2.35.4.0", {"center": v(401.95, 193.68) * mm, "radius": 9.53 * mm});
            skCircle(sketch, "E2.35.5.0", {"center": v(401.95, 169.55) * mm, "radius": 9.53 * mm});
            skCircle(sketch, "E2.35.6.0", {"center": v(401.95, 145.42) * mm, "radius": 9.53 * mm});
            skCircle(sketch, "E2.35.7.0", {"center": v(401.95, 121.29) * mm, "radius": 9.53 * mm});
            skCircle(sketch, "E2.35.8.0", {"center": v(401.95, 97.16) * mm, "radius": 9.53 * mm});
            skCircle(sketch, "E2.35.9.0", {"center": v(401.95, 73.03) * mm, "radius": 9.53 * mm});
            skCircle(sketch, "E2.35.10.0", {"center": v(401.95, 48.9) * mm, "radius": 9.53 * mm});
            skCircle(sketch, "E2.35.11.0", {"center": v(401.95, 24.77) * mm, "radius": 9.53 * mm});
            skCircle(sketch, "E2.35.12.0", {"center": v(401.95, 0.64) * mm, "radius": 9.53 * mm});
            skCircle(sketch, "E2.35.13.0", {"center": v(401.95, -23.5) * mm, "radius": 9.53 * mm});
            skCircle(sketch, "E2.35.14.0", {"center": v(401.95, -47.62) * mm, "radius": 9.53 * mm});
            skCircle(sketch, "E2.35.15.0", {"center": v(401.95, -71.75) * mm, "radius": 9.53 * mm});
            skCircle(sketch, "E2.35.16.0", {"center": v(401.95, -95.88) * mm, "radius": 9.53 * mm});
            skCircle(sketch, "E2.35.17.0", {"center": v(401.95, -120.01) * mm, "radius": 9.53 * mm});
            skCircle(sketch, "E2.35.18.0", {"center": v(401.95, -144.14) * mm, "radius": 9.53 * mm});
            skCircle(sketch, "E2.35.19.0", {"center": v(401.95, -168.27) * mm, "radius": 9.53 * mm});
            skCircle(sketch, "E2.35.20.0", {"center": v(401.95, -192.4) * mm, "radius": 9.53 * mm});
            skCircle(sketch, "E2.35.21.0", {"center": v(401.95, -216.53) * mm, "radius": 9.53 * mm});
            skCircle(sketch, "E2.35.22.0", {"center": v(401.95, -240.66) * mm, "radius": 9.53 * mm});
            skCircle(sketch, "E2.35.23.0", {"center": v(401.95, -264.8) * mm, "radius": 9.53 * mm});
            skCircle(sketch, "E2.35.24.0", {"center": v(401.95, -288.92) * mm, "radius": 9.53 * mm});
            skCircle(sketch, "E2.36.0.0", {"center": v(426.08, 290.2) * mm, "radius": 9.53 * mm});
            skCircle(sketch, "E2.36.1.0", {"center": v(426.08, 266.07) * mm, "radius": 9.53 * mm});
            skCircle(sketch, "E2.36.2.0", {"center": v(426.08, 241.94) * mm, "radius": 9.53 * mm});
            skCircle(sketch, "E2.36.3.0", {"center": v(426.08, 217.8) * mm, "radius": 9.53 * mm});
            skCircle(sketch, "E2.36.4.0", {"center": v(426.08, 193.68) * mm, "radius": 9.53 * mm});
            skCircle(sketch, "E2.36.5.0", {"center": v(426.08, 169.55) * mm, "radius": 9.53 * mm});
            skCircle(sketch, "E2.36.6.0", {"center": v(426.08, 145.42) * mm, "radius": 9.53 * mm});
            skCircle(sketch, "E2.36.7.0", {"center": v(426.08, 121.29) * mm, "radius": 9.53 * mm});
            skCircle(sketch, "E2.36.8.0", {"center": v(426.08, 97.16) * mm, "radius": 9.53 * mm});
            skCircle(sketch, "E2.36.9.0", {"center": v(426.08, 73.03) * mm, "radius": 9.53 * mm});
            skCircle(sketch, "E2.36.10.0", {"center": v(426.08, 48.9) * mm, "radius": 9.53 * mm});
            skCircle(sketch, "E2.36.11.0", {"center": v(426.08, 24.77) * mm, "radius": 9.53 * mm});
            skCircle(sketch, "E2.36.12.0", {"center": v(426.08, 0.64) * mm, "radius": 9.53 * mm});
            skCircle(sketch, "E2.36.13.0", {"center": v(426.08, -23.5) * mm, "radius": 9.53 * mm});
            skCircle(sketch, "E2.36.14.0", {"center": v(426.08, -47.62) * mm, "radius": 9.53 * mm});
            skCircle(sketch, "E2.36.15.0", {"center": v(426.08, -71.75) * mm, "radius": 9.53 * mm});
            skCircle(sketch, "E2.36.16.0", {"center": v(426.08, -95.88) * mm, "radius": 9.53 * mm});
            skCircle(sketch, "E2.36.17.0", {"center": v(426.08, -120.01) * mm, "radius": 9.53 * mm});
            skCircle(sketch, "E2.36.18.0", {"center": v(426.08, -144.14) * mm, "radius": 9.53 * mm});
            skCircle(sketch, "E2.36.19.0", {"center": v(426.08, -168.27) * mm, "radius": 9.53 * mm});
            skCircle(sketch, "E2.36.20.0", {"center": v(426.08, -192.4) * mm, "radius": 9.53 * mm});
            skCircle(sketch, "E2.36.21.0", {"center": v(426.08, -216.53) * mm, "radius": 9.53 * mm});
            skCircle(sketch, "E2.36.22.0", {"center": v(426.08, -240.66) * mm, "radius": 9.53 * mm});
            skCircle(sketch, "E2.36.23.0", {"center": v(426.08, -264.8) * mm, "radius": 9.53 * mm});
            skCircle(sketch, "E2.36.24.0", {"center": v(426.08, -288.92) * mm, "radius": 9.53 * mm});
            skLineSegment(sketch, "E2.direction1", {"start": v(-442.6, 290.2) * mm, "end": v(-418.47, 290.2) * mm, "construction": true});
            skLineSegment(sketch, "E2.direction2", {"start": v(-442.6, 290.2) * mm, "end": v(-442.6, 266.07) * mm, "construction": true});
            skSolve(sketch);
        }
        {
            var Q0;
            Q0 = qSketchRegion(id + "F0", true);
            extrude(context, id + "F1", {"entities" : qUnion([Q0]), "depth" : 1 * mm, "offsetDistance" : 25.4 * mm});
        }
    });
